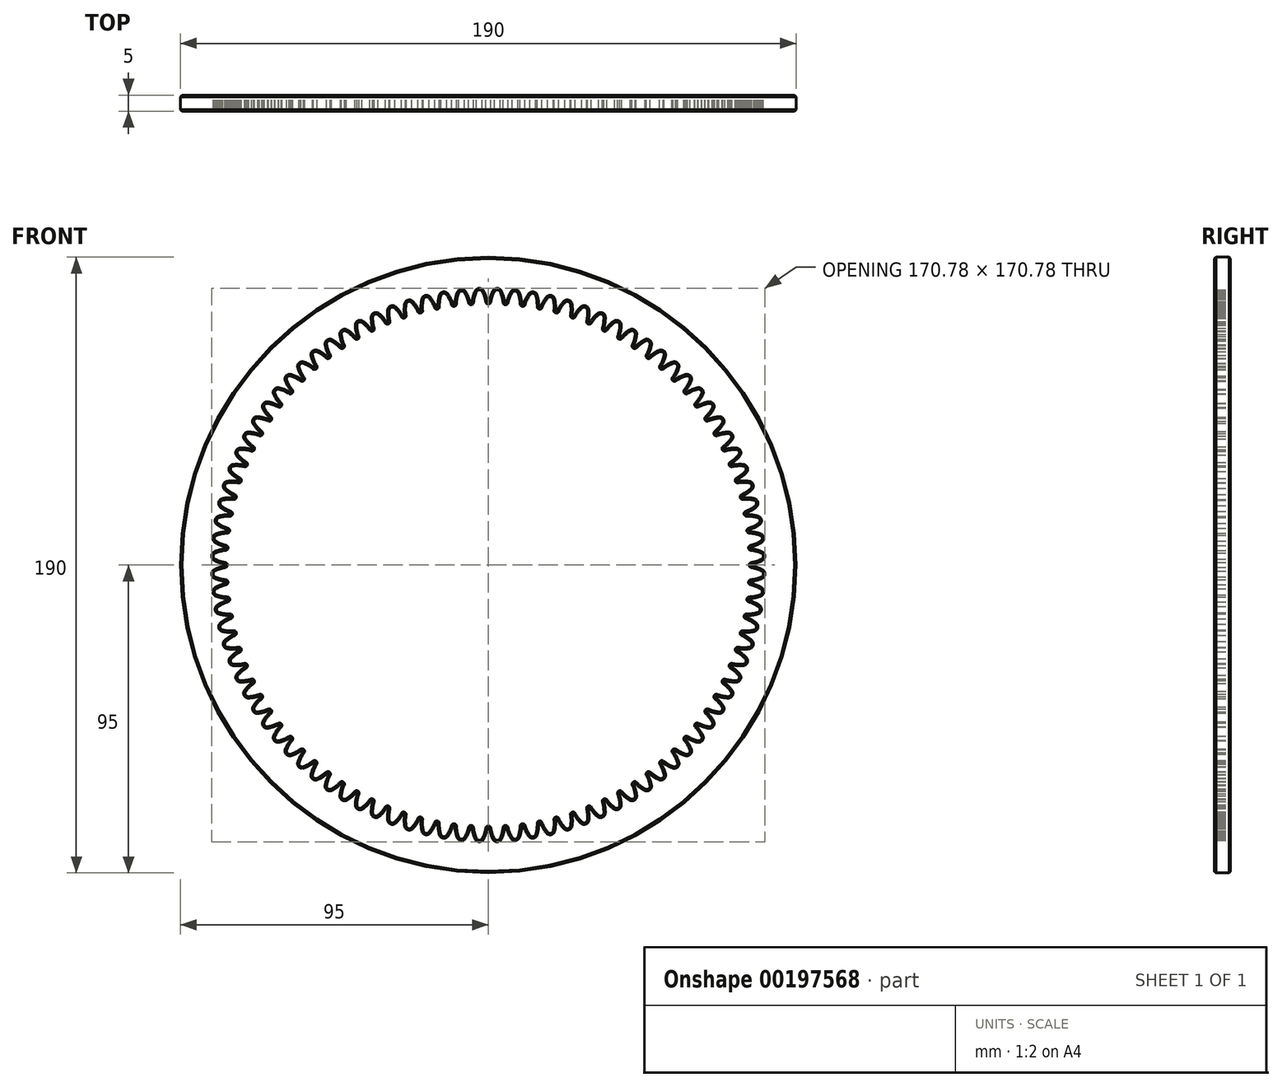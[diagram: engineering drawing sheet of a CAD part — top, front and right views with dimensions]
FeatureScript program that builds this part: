
annotation { "Feature Type Name" : "Feature", "Feature Type Description" : "" }
export const myFeature = defineFeature(function(context is Context, id is Id, definition is map)
    precondition{}
    {
        {
            var Q0;
            Q0=qCreatedBy(makeId("Front.planeOp"),FACE);
            var sketch = newSketch(context, id + "F0", { "sketchPlane" : qUnion([Q0])});
            skArc(sketch, "E0.1.2", {"start": v(-3.67, 84.28) * mm, "mid": v(-4.24, 82.62) * mm, "end": v(-4.54, 80.9) * mm});
            skArc(sketch, "E1.MirrorCS", {"start": v(-1.85, 84.33) * mm, "mid": v(-1.17, 82.72) * mm, "end": v(-0.76, 81.02) * mm});
            skArc(sketch, "E2", {"start": v(-0.76, 81.02) * mm, "mid": v(0, 80.48) * mm, "end": v(0.76, 81.02) * mm});
            skArc(sketch, "E3", {"start": v(-1.85, 84.33) * mm, "mid": v(-2.78, 84.9) * mm, "end": v(-3.67, 84.28) * mm});
            skArc(sketch, "E4.1.0", {"start": v(-6.06, 80.8) * mm, "mid": v(-5.26, 80.3) * mm, "end": v(-4.54, 80.9) * mm});
            skArc(sketch, "E4.1.1", {"start": v(-9.17, 83.85) * mm, "mid": v(-9.64, 82.17) * mm, "end": v(-9.82, 80.43) * mm});
            skArc(sketch, "E4.1.2", {"start": v(-7.36, 84.03) * mm, "mid": v(-6.58, 82.47) * mm, "end": v(-6.06, 80.8) * mm});
            skArc(sketch, "E4.1.3", {"start": v(-7.36, 84.03) * mm, "mid": v(-8.33, 84.53) * mm, "end": v(-9.17, 83.85) * mm});
            skArc(sketch, "E4.2.0", {"start": v(-11.33, 80.23) * mm, "mid": v(-10.5, 79.79) * mm, "end": v(-9.82, 80.43) * mm});
            skArc(sketch, "E4.2.1", {"start": v(-14.64, 83.08) * mm, "mid": v(-14.99, 81.36) * mm, "end": v(-15.06, 79.62) * mm});
            skArc(sketch, "E4.2.2", {"start": v(-12.84, 83.37) * mm, "mid": v(-11.96, 81.86) * mm, "end": v(-11.33, 80.23) * mm});
            skArc(sketch, "E4.2.3", {"start": v(-12.84, 83.37) * mm, "mid": v(-13.84, 83.8) * mm, "end": v(-14.64, 83.08) * mm});
            skArc(sketch, "E4.3.0", {"start": v(-16.56, 79.32) * mm, "mid": v(-15.7, 78.93) * mm, "end": v(-15.06, 79.62) * mm});
            skArc(sketch, "E4.3.1", {"start": v(-20.04, 81.94) * mm, "mid": v(-20.28, 80.2) * mm, "end": v(-20.23, 78.46) * mm});
            skArc(sketch, "E4.3.2", {"start": v(-18.27, 82.35) * mm, "mid": v(-17.29, 80.9) * mm, "end": v(-16.56, 79.32) * mm});
            skArc(sketch, "E4.3.3", {"start": v(-18.27, 82.35) * mm, "mid": v(-19.29, 82.72) * mm, "end": v(-20.04, 81.94) * mm});
            skArc(sketch, "E4.4.0", {"start": v(-21.7, 78.07) * mm, "mid": v(-20.83, 77.73) * mm, "end": v(-20.23, 78.46) * mm});
            skArc(sketch, "E4.4.1", {"start": v(-25.35, 80.45) * mm, "mid": v(-25.48, 78.71) * mm, "end": v(-25.32, 76.97) * mm});
            skArc(sketch, "E4.4.2", {"start": v(-23.62, 80.98) * mm, "mid": v(-22.54, 79.6) * mm, "end": v(-21.7, 78.07) * mm});
            skArc(sketch, "E4.4.3", {"start": v(-23.62, 80.98) * mm, "mid": v(-24.66, 81.28) * mm, "end": v(-25.35, 80.45) * mm});
            skArc(sketch, "E4.5.0", {"start": v(-26.77, 76.48) * mm, "mid": v(-25.87, 76.2) * mm, "end": v(-25.32, 76.97) * mm});
            skArc(sketch, "E4.5.1", {"start": v(-30.56, 78.62) * mm, "mid": v(-30.58, 76.88) * mm, "end": v(-30.3, 75.15) * mm});
            skArc(sketch, "E4.5.2", {"start": v(-28.86, 79.26) * mm, "mid": v(-27.7, 77.96) * mm, "end": v(-26.77, 76.48) * mm});
            skArc(sketch, "E4.5.3", {"start": v(-28.86, 79.26) * mm, "mid": v(-29.92, 79.5) * mm, "end": v(-30.56, 78.62) * mm});
            skArc(sketch, "E4.6.0", {"start": v(-31.71, 74.56) * mm, "mid": v(-30.8, 74.35) * mm, "end": v(-30.3, 75.15) * mm});
            skArc(sketch, "E4.6.1", {"start": v(-35.64, 76.46) * mm, "mid": v(-35.54, 74.71) * mm, "end": v(-35.15, 73) * mm});
            skArc(sketch, "E4.6.2", {"start": v(-33.99, 77.2) * mm, "mid": v(-32.74, 75.98) * mm, "end": v(-31.71, 74.56) * mm});
            skArc(sketch, "E4.6.3", {"start": v(-33.99, 77.2) * mm, "mid": v(-35.05, 77.37) * mm, "end": v(-35.64, 76.46) * mm});
            skArc(sketch, "E4.7.0", {"start": v(-36.52, 72.33) * mm, "mid": v(-35.6, 72.18) * mm, "end": v(-35.15, 73) * mm});
            skArc(sketch, "E4.7.1", {"start": v(-40.56, 73.96) * mm, "mid": v(-40.35, 72.23) * mm, "end": v(-39.85, 70.55) * mm});
            skArc(sketch, "E4.7.2", {"start": v(-38.96, 74.82) * mm, "mid": v(-37.64, 73.68) * mm, "end": v(-36.52, 72.33) * mm});
            skArc(sketch, "E4.7.3", {"start": v(-38.96, 74.82) * mm, "mid": v(-40.04, 74.9) * mm, "end": v(-40.56, 73.96) * mm});
            skArc(sketch, "E4.8.0", {"start": v(-41.17, 69.79) * mm, "mid": v(-40.24, 69.7) * mm, "end": v(-39.85, 70.55) * mm});
            skArc(sketch, "E4.8.1", {"start": v(-45.31, 71.15) * mm, "mid": v(-44.99, 69.43) * mm, "end": v(-44.38, 67.8) * mm});
            skArc(sketch, "E4.8.2", {"start": v(-43.77, 72.1) * mm, "mid": v(-42.38, 71.06) * mm, "end": v(-41.17, 69.79) * mm});
            skArc(sketch, "E4.8.3", {"start": v(-43.77, 72.1) * mm, "mid": v(-44.85, 72.13) * mm, "end": v(-45.31, 71.15) * mm});
            skArc(sketch, "E4.9.0", {"start": v(-45.65, 66.94) * mm, "mid": v(-44.7, 66.91) * mm, "end": v(-44.38, 67.8) * mm});
            skArc(sketch, "E4.9.1", {"start": v(-49.87, 68.04) * mm, "mid": v(-49.43, 66.34) * mm, "end": v(-48.72, 64.75) * mm});
            skArc(sketch, "E4.9.2", {"start": v(-48.4, 69.1) * mm, "mid": v(-46.93, 68.13) * mm, "end": v(-45.65, 66.94) * mm});
            skArc(sketch, "E4.9.3", {"start": v(-48.4, 69.1) * mm, "mid": v(-49.47, 69.04) * mm, "end": v(-49.87, 68.04) * mm});
            skArc(sketch, "E4.10.0", {"start": v(-49.93, 63.82) * mm, "mid": v(-49, 63.85) * mm, "end": v(-48.72, 64.75) * mm});
            skArc(sketch, "E4.10.1", {"start": v(-54.21, 64.63) * mm, "mid": v(-53.66, 62.97) * mm, "end": v(-52.85, 61.42) * mm});
            skArc(sketch, "E4.10.2", {"start": v(-52.8, 65.78) * mm, "mid": v(-51.29, 64.92) * mm, "end": v(-49.93, 63.82) * mm});
            skArc(sketch, "E4.10.3", {"start": v(-52.8, 65.78) * mm, "mid": v(-53.88, 65.66) * mm, "end": v(-54.21, 64.63) * mm});
            skArc(sketch, "E4.11.0", {"start": v(-54, 60.41) * mm, "mid": v(-53.06, 60.5) * mm, "end": v(-52.85, 61.42) * mm});
            skArc(sketch, "E4.11.1", {"start": v(-58.32, 60.94) * mm, "mid": v(-57.67, 59.32) * mm, "end": v(-56.75, 57.83) * mm});
            skArc(sketch, "E4.11.2", {"start": v(-57, 62.18) * mm, "mid": v(-55.43, 61.42) * mm, "end": v(-54, 60.41) * mm});
            skArc(sketch, "E4.11.3", {"start": v(-57, 62.18) * mm, "mid": v(-58.06, 62) * mm, "end": v(-58.32, 60.94) * mm});
            skArc(sketch, "E4.12.0", {"start": v(-57.83, 56.75) * mm, "mid": v(-56.9, 56.9) * mm, "end": v(-56.75, 57.83) * mm});
            skArc(sketch, "E4.12.1", {"start": v(-62.18, 57) * mm, "mid": v(-61.42, 55.43) * mm, "end": v(-60.41, 54) * mm});
            skArc(sketch, "E4.12.2", {"start": v(-60.94, 58.32) * mm, "mid": v(-59.32, 57.67) * mm, "end": v(-57.83, 56.75) * mm});
            skArc(sketch, "E4.12.3", {"start": v(-60.94, 58.32) * mm, "mid": v(-62, 58.06) * mm, "end": v(-62.18, 57) * mm});
            skArc(sketch, "E4.13.0", {"start": v(-61.42, 52.85) * mm, "mid": v(-60.5, 53.06) * mm, "end": v(-60.41, 54) * mm});
            skArc(sketch, "E4.13.1", {"start": v(-65.78, 52.8) * mm, "mid": v(-64.92, 51.29) * mm, "end": v(-63.82, 49.93) * mm});
            skArc(sketch, "E4.13.2", {"start": v(-64.63, 54.21) * mm, "mid": v(-62.97, 53.66) * mm, "end": v(-61.42, 52.85) * mm});
            skArc(sketch, "E4.13.3", {"start": v(-64.63, 54.21) * mm, "mid": v(-65.66, 53.88) * mm, "end": v(-65.78, 52.8) * mm});
            skArc(sketch, "E4.14.0", {"start": v(-64.75, 48.72) * mm, "mid": v(-63.85, 49) * mm, "end": v(-63.82, 49.93) * mm});
            skArc(sketch, "E4.14.1", {"start": v(-69.1, 48.4) * mm, "mid": v(-68.13, 46.93) * mm, "end": v(-66.94, 45.65) * mm});
            skArc(sketch, "E4.14.2", {"start": v(-68.04, 49.87) * mm, "mid": v(-66.34, 49.43) * mm, "end": v(-64.75, 48.72) * mm});
            skArc(sketch, "E4.14.3", {"start": v(-68.04, 49.87) * mm, "mid": v(-69.04, 49.47) * mm, "end": v(-69.1, 48.4) * mm});
            skArc(sketch, "E4.15.0", {"start": v(-67.8, 44.38) * mm, "mid": v(-66.91, 44.7) * mm, "end": v(-66.94, 45.65) * mm});
            skArc(sketch, "E4.15.1", {"start": v(-72.1, 43.77) * mm, "mid": v(-71.06, 42.38) * mm, "end": v(-69.79, 41.17) * mm});
            skArc(sketch, "E4.15.2", {"start": v(-71.15, 45.31) * mm, "mid": v(-69.43, 44.99) * mm, "end": v(-67.8, 44.38) * mm});
            skArc(sketch, "E4.15.3", {"start": v(-71.15, 45.31) * mm, "mid": v(-72.13, 44.85) * mm, "end": v(-72.1, 43.77) * mm});
            skArc(sketch, "E4.16.0", {"start": v(-70.55, 39.85) * mm, "mid": v(-69.7, 40.24) * mm, "end": v(-69.79, 41.17) * mm});
            skArc(sketch, "E4.16.1", {"start": v(-74.82, 38.96) * mm, "mid": v(-73.68, 37.64) * mm, "end": v(-72.33, 36.52) * mm});
            skArc(sketch, "E4.16.2", {"start": v(-73.96, 40.56) * mm, "mid": v(-72.23, 40.35) * mm, "end": v(-70.55, 39.85) * mm});
            skArc(sketch, "E4.16.3", {"start": v(-73.96, 40.56) * mm, "mid": v(-74.9, 40.04) * mm, "end": v(-74.82, 38.96) * mm});
            skArc(sketch, "E4.17.0", {"start": v(-73, 35.15) * mm, "mid": v(-72.18, 35.6) * mm, "end": v(-72.33, 36.52) * mm});
            skArc(sketch, "E4.17.1", {"start": v(-77.2, 33.99) * mm, "mid": v(-75.98, 32.74) * mm, "end": v(-74.56, 31.71) * mm});
            skArc(sketch, "E4.17.2", {"start": v(-76.46, 35.64) * mm, "mid": v(-74.71, 35.54) * mm, "end": v(-73, 35.15) * mm});
            skArc(sketch, "E4.17.3", {"start": v(-76.46, 35.64) * mm, "mid": v(-77.37, 35.05) * mm, "end": v(-77.2, 33.99) * mm});
            skArc(sketch, "E4.18.0", {"start": v(-75.15, 30.3) * mm, "mid": v(-74.35, 30.8) * mm, "end": v(-74.56, 31.71) * mm});
            skArc(sketch, "E4.18.1", {"start": v(-79.26, 28.86) * mm, "mid": v(-77.96, 27.7) * mm, "end": v(-76.48, 26.77) * mm});
            skArc(sketch, "E4.18.2", {"start": v(-78.62, 30.56) * mm, "mid": v(-76.88, 30.58) * mm, "end": v(-75.15, 30.3) * mm});
            skArc(sketch, "E4.18.3", {"start": v(-78.62, 30.56) * mm, "mid": v(-79.5, 29.92) * mm, "end": v(-79.26, 28.86) * mm});
            skArc(sketch, "E4.19.0", {"start": v(-76.97, 25.32) * mm, "mid": v(-76.2, 25.87) * mm, "end": v(-76.48, 26.77) * mm});
            skArc(sketch, "E4.19.1", {"start": v(-80.98, 23.62) * mm, "mid": v(-79.6, 22.54) * mm, "end": v(-78.07, 21.7) * mm});
            skArc(sketch, "E4.19.2", {"start": v(-80.45, 25.35) * mm, "mid": v(-78.71, 25.48) * mm, "end": v(-76.97, 25.32) * mm});
            skArc(sketch, "E4.19.3", {"start": v(-80.45, 25.35) * mm, "mid": v(-81.28, 24.66) * mm, "end": v(-80.98, 23.62) * mm});
            skArc(sketch, "E4.20.0", {"start": v(-78.46, 20.23) * mm, "mid": v(-77.73, 20.83) * mm, "end": v(-78.07, 21.7) * mm});
            skArc(sketch, "E4.20.1", {"start": v(-82.35, 18.27) * mm, "mid": v(-80.9, 17.29) * mm, "end": v(-79.32, 16.56) * mm});
            skArc(sketch, "E4.20.2", {"start": v(-81.94, 20.04) * mm, "mid": v(-80.2, 20.28) * mm, "end": v(-78.46, 20.23) * mm});
            skArc(sketch, "E4.20.3", {"start": v(-81.94, 20.04) * mm, "mid": v(-82.72, 19.29) * mm, "end": v(-82.35, 18.27) * mm});
            skArc(sketch, "E4.21.0", {"start": v(-79.62, 15.06) * mm, "mid": v(-78.93, 15.7) * mm, "end": v(-79.32, 16.56) * mm});
            skArc(sketch, "E4.21.1", {"start": v(-83.37, 12.84) * mm, "mid": v(-81.86, 11.96) * mm, "end": v(-80.23, 11.33) * mm});
            skArc(sketch, "E4.21.2", {"start": v(-83.08, 14.64) * mm, "mid": v(-81.36, 14.99) * mm, "end": v(-79.62, 15.06) * mm});
            skArc(sketch, "E4.21.3", {"start": v(-83.08, 14.64) * mm, "mid": v(-83.8, 13.84) * mm, "end": v(-83.37, 12.84) * mm});
            skArc(sketch, "E4.22.0", {"start": v(-80.43, 9.82) * mm, "mid": v(-79.79, 10.5) * mm, "end": v(-80.23, 11.33) * mm});
            skArc(sketch, "E4.22.1", {"start": v(-84.03, 7.36) * mm, "mid": v(-82.47, 6.58) * mm, "end": v(-80.8, 6.06) * mm});
            skArc(sketch, "E4.22.2", {"start": v(-83.85, 9.17) * mm, "mid": v(-82.17, 9.64) * mm, "end": v(-80.43, 9.82) * mm});
            skArc(sketch, "E4.22.3", {"start": v(-83.85, 9.17) * mm, "mid": v(-84.53, 8.33) * mm, "end": v(-84.03, 7.36) * mm});
            skArc(sketch, "E4.23.0", {"start": v(-80.9, 4.54) * mm, "mid": v(-80.3, 5.26) * mm, "end": v(-80.8, 6.06) * mm});
            skArc(sketch, "E4.23.1", {"start": v(-84.33, 1.85) * mm, "mid": v(-82.72, 1.17) * mm, "end": v(-81.02, 0.76) * mm});
            skArc(sketch, "E4.23.2", {"start": v(-84.28, 3.67) * mm, "mid": v(-82.62, 4.24) * mm, "end": v(-80.9, 4.54) * mm});
            skArc(sketch, "E4.23.3", {"start": v(-84.28, 3.67) * mm, "mid": v(-84.9, 2.78) * mm, "end": v(-84.33, 1.85) * mm});
            skArc(sketch, "E4.24.0", {"start": v(-81.02, -0.76) * mm, "mid": v(-80.48, 0) * mm, "end": v(-81.02, 0.76) * mm});
            skArc(sketch, "E4.24.1", {"start": v(-84.28, -3.67) * mm, "mid": v(-82.62, -4.24) * mm, "end": v(-80.9, -4.54) * mm});
            skArc(sketch, "E4.24.2", {"start": v(-84.33, -1.85) * mm, "mid": v(-82.72, -1.17) * mm, "end": v(-81.02, -0.76) * mm});
            skArc(sketch, "E4.24.3", {"start": v(-84.33, -1.85) * mm, "mid": v(-84.9, -2.78) * mm, "end": v(-84.28, -3.67) * mm});
            skArc(sketch, "E4.25.0", {"start": v(-80.8, -6.06) * mm, "mid": v(-80.3, -5.26) * mm, "end": v(-80.9, -4.54) * mm});
            skArc(sketch, "E4.25.1", {"start": v(-83.85, -9.17) * mm, "mid": v(-82.17, -9.64) * mm, "end": v(-80.43, -9.82) * mm});
            skArc(sketch, "E4.25.2", {"start": v(-84.03, -7.36) * mm, "mid": v(-82.47, -6.58) * mm, "end": v(-80.8, -6.06) * mm});
            skArc(sketch, "E4.25.3", {"start": v(-84.03, -7.36) * mm, "mid": v(-84.53, -8.33) * mm, "end": v(-83.85, -9.17) * mm});
            skArc(sketch, "E4.26.0", {"start": v(-80.23, -11.33) * mm, "mid": v(-79.79, -10.5) * mm, "end": v(-80.43, -9.82) * mm});
            skArc(sketch, "E4.26.1", {"start": v(-83.08, -14.64) * mm, "mid": v(-81.36, -14.99) * mm, "end": v(-79.62, -15.06) * mm});
            skArc(sketch, "E4.26.2", {"start": v(-83.37, -12.84) * mm, "mid": v(-81.86, -11.96) * mm, "end": v(-80.23, -11.33) * mm});
            skArc(sketch, "E4.26.3", {"start": v(-83.37, -12.84) * mm, "mid": v(-83.8, -13.84) * mm, "end": v(-83.08, -14.64) * mm});
            skArc(sketch, "E4.27.0", {"start": v(-79.32, -16.56) * mm, "mid": v(-78.93, -15.7) * mm, "end": v(-79.62, -15.06) * mm});
            skArc(sketch, "E4.27.1", {"start": v(-81.94, -20.04) * mm, "mid": v(-80.2, -20.28) * mm, "end": v(-78.46, -20.23) * mm});
            skArc(sketch, "E4.27.2", {"start": v(-82.35, -18.27) * mm, "mid": v(-80.9, -17.29) * mm, "end": v(-79.32, -16.56) * mm});
            skArc(sketch, "E4.27.3", {"start": v(-82.35, -18.27) * mm, "mid": v(-82.72, -19.29) * mm, "end": v(-81.94, -20.04) * mm});
            skArc(sketch, "E4.28.0", {"start": v(-78.07, -21.7) * mm, "mid": v(-77.73, -20.83) * mm, "end": v(-78.46, -20.23) * mm});
            skArc(sketch, "E4.28.1", {"start": v(-80.45, -25.35) * mm, "mid": v(-78.71, -25.48) * mm, "end": v(-76.97, -25.32) * mm});
            skArc(sketch, "E4.28.2", {"start": v(-80.98, -23.62) * mm, "mid": v(-79.6, -22.54) * mm, "end": v(-78.07, -21.7) * mm});
            skArc(sketch, "E4.28.3", {"start": v(-80.98, -23.62) * mm, "mid": v(-81.28, -24.66) * mm, "end": v(-80.45, -25.35) * mm});
            skArc(sketch, "E4.29.0", {"start": v(-76.48, -26.77) * mm, "mid": v(-76.2, -25.87) * mm, "end": v(-76.97, -25.32) * mm});
            skArc(sketch, "E4.29.1", {"start": v(-78.62, -30.56) * mm, "mid": v(-76.88, -30.58) * mm, "end": v(-75.15, -30.3) * mm});
            skArc(sketch, "E4.29.2", {"start": v(-79.26, -28.86) * mm, "mid": v(-77.96, -27.7) * mm, "end": v(-76.48, -26.77) * mm});
            skArc(sketch, "E4.29.3", {"start": v(-79.26, -28.86) * mm, "mid": v(-79.5, -29.92) * mm, "end": v(-78.62, -30.56) * mm});
            skArc(sketch, "E4.30.0", {"start": v(-74.56, -31.71) * mm, "mid": v(-74.35, -30.8) * mm, "end": v(-75.15, -30.3) * mm});
            skArc(sketch, "E4.30.1", {"start": v(-76.46, -35.64) * mm, "mid": v(-74.71, -35.54) * mm, "end": v(-73, -35.15) * mm});
            skArc(sketch, "E4.30.2", {"start": v(-77.2, -33.99) * mm, "mid": v(-75.98, -32.74) * mm, "end": v(-74.56, -31.71) * mm});
            skArc(sketch, "E4.30.3", {"start": v(-77.2, -33.99) * mm, "mid": v(-77.37, -35.05) * mm, "end": v(-76.46, -35.64) * mm});
            skArc(sketch, "E4.31.0", {"start": v(-72.33, -36.52) * mm, "mid": v(-72.18, -35.6) * mm, "end": v(-73, -35.15) * mm});
            skArc(sketch, "E4.31.1", {"start": v(-73.96, -40.56) * mm, "mid": v(-72.23, -40.35) * mm, "end": v(-70.55, -39.85) * mm});
            skArc(sketch, "E4.31.2", {"start": v(-74.82, -38.96) * mm, "mid": v(-73.68, -37.64) * mm, "end": v(-72.33, -36.52) * mm});
            skArc(sketch, "E4.31.3", {"start": v(-74.82, -38.96) * mm, "mid": v(-74.9, -40.04) * mm, "end": v(-73.96, -40.56) * mm});
            skArc(sketch, "E4.32.0", {"start": v(-69.79, -41.17) * mm, "mid": v(-69.7, -40.24) * mm, "end": v(-70.55, -39.85) * mm});
            skArc(sketch, "E4.32.1", {"start": v(-71.15, -45.31) * mm, "mid": v(-69.43, -44.99) * mm, "end": v(-67.8, -44.38) * mm});
            skArc(sketch, "E4.32.2", {"start": v(-72.1, -43.77) * mm, "mid": v(-71.06, -42.38) * mm, "end": v(-69.79, -41.17) * mm});
            skArc(sketch, "E4.32.3", {"start": v(-72.1, -43.77) * mm, "mid": v(-72.13, -44.85) * mm, "end": v(-71.15, -45.31) * mm});
            skArc(sketch, "E4.33.0", {"start": v(-66.94, -45.65) * mm, "mid": v(-66.91, -44.7) * mm, "end": v(-67.8, -44.38) * mm});
            skArc(sketch, "E4.33.1", {"start": v(-68.04, -49.87) * mm, "mid": v(-66.34, -49.43) * mm, "end": v(-64.75, -48.72) * mm});
            skArc(sketch, "E4.33.2", {"start": v(-69.1, -48.4) * mm, "mid": v(-68.13, -46.93) * mm, "end": v(-66.94, -45.65) * mm});
            skArc(sketch, "E4.33.3", {"start": v(-69.1, -48.4) * mm, "mid": v(-69.04, -49.47) * mm, "end": v(-68.04, -49.87) * mm});
            skArc(sketch, "E4.34.0", {"start": v(-63.82, -49.93) * mm, "mid": v(-63.85, -49) * mm, "end": v(-64.75, -48.72) * mm});
            skArc(sketch, "E4.34.1", {"start": v(-64.63, -54.21) * mm, "mid": v(-62.97, -53.66) * mm, "end": v(-61.42, -52.85) * mm});
            skArc(sketch, "E4.34.2", {"start": v(-65.78, -52.8) * mm, "mid": v(-64.92, -51.29) * mm, "end": v(-63.82, -49.93) * mm});
            skArc(sketch, "E4.34.3", {"start": v(-65.78, -52.8) * mm, "mid": v(-65.66, -53.88) * mm, "end": v(-64.63, -54.21) * mm});
            skArc(sketch, "E4.35.0", {"start": v(-60.41, -54) * mm, "mid": v(-60.5, -53.06) * mm, "end": v(-61.42, -52.85) * mm});
            skArc(sketch, "E4.35.1", {"start": v(-60.94, -58.32) * mm, "mid": v(-59.32, -57.67) * mm, "end": v(-57.83, -56.75) * mm});
            skArc(sketch, "E4.35.2", {"start": v(-62.18, -57) * mm, "mid": v(-61.42, -55.43) * mm, "end": v(-60.41, -54) * mm});
            skArc(sketch, "E4.35.3", {"start": v(-62.18, -57) * mm, "mid": v(-62, -58.06) * mm, "end": v(-60.94, -58.32) * mm});
            skArc(sketch, "E4.36.0", {"start": v(-56.75, -57.83) * mm, "mid": v(-56.9, -56.9) * mm, "end": v(-57.83, -56.75) * mm});
            skArc(sketch, "E4.36.1", {"start": v(-57, -62.18) * mm, "mid": v(-55.43, -61.42) * mm, "end": v(-54, -60.41) * mm});
            skArc(sketch, "E4.36.2", {"start": v(-58.32, -60.94) * mm, "mid": v(-57.67, -59.32) * mm, "end": v(-56.75, -57.83) * mm});
            skArc(sketch, "E4.36.3", {"start": v(-58.32, -60.94) * mm, "mid": v(-58.06, -62) * mm, "end": v(-57, -62.18) * mm});
            skArc(sketch, "E4.37.0", {"start": v(-52.85, -61.42) * mm, "mid": v(-53.06, -60.5) * mm, "end": v(-54, -60.41) * mm});
            skArc(sketch, "E4.37.1", {"start": v(-52.8, -65.78) * mm, "mid": v(-51.29, -64.92) * mm, "end": v(-49.93, -63.82) * mm});
            skArc(sketch, "E4.37.2", {"start": v(-54.21, -64.63) * mm, "mid": v(-53.66, -62.97) * mm, "end": v(-52.85, -61.42) * mm});
            skArc(sketch, "E4.37.3", {"start": v(-54.21, -64.63) * mm, "mid": v(-53.88, -65.66) * mm, "end": v(-52.8, -65.78) * mm});
            skArc(sketch, "E4.38.0", {"start": v(-48.72, -64.75) * mm, "mid": v(-49, -63.85) * mm, "end": v(-49.93, -63.82) * mm});
            skArc(sketch, "E4.38.1", {"start": v(-48.4, -69.1) * mm, "mid": v(-46.93, -68.13) * mm, "end": v(-45.65, -66.94) * mm});
            skArc(sketch, "E4.38.2", {"start": v(-49.87, -68.04) * mm, "mid": v(-49.43, -66.34) * mm, "end": v(-48.72, -64.75) * mm});
            skArc(sketch, "E4.38.3", {"start": v(-49.87, -68.04) * mm, "mid": v(-49.47, -69.04) * mm, "end": v(-48.4, -69.1) * mm});
            skArc(sketch, "E4.39.0", {"start": v(-44.38, -67.8) * mm, "mid": v(-44.7, -66.91) * mm, "end": v(-45.65, -66.94) * mm});
            skArc(sketch, "E4.39.1", {"start": v(-43.77, -72.1) * mm, "mid": v(-42.38, -71.06) * mm, "end": v(-41.17, -69.79) * mm});
            skArc(sketch, "E4.39.2", {"start": v(-45.31, -71.15) * mm, "mid": v(-44.99, -69.43) * mm, "end": v(-44.38, -67.8) * mm});
            skArc(sketch, "E4.39.3", {"start": v(-45.31, -71.15) * mm, "mid": v(-44.85, -72.13) * mm, "end": v(-43.77, -72.1) * mm});
            skArc(sketch, "E4.40.0", {"start": v(-39.85, -70.55) * mm, "mid": v(-40.24, -69.7) * mm, "end": v(-41.17, -69.79) * mm});
            skArc(sketch, "E4.40.1", {"start": v(-38.96, -74.82) * mm, "mid": v(-37.64, -73.68) * mm, "end": v(-36.52, -72.33) * mm});
            skArc(sketch, "E4.40.2", {"start": v(-40.56, -73.96) * mm, "mid": v(-40.35, -72.23) * mm, "end": v(-39.85, -70.55) * mm});
            skArc(sketch, "E4.40.3", {"start": v(-40.56, -73.96) * mm, "mid": v(-40.04, -74.9) * mm, "end": v(-38.96, -74.82) * mm});
            skArc(sketch, "E4.41.0", {"start": v(-35.15, -73) * mm, "mid": v(-35.6, -72.18) * mm, "end": v(-36.52, -72.33) * mm});
            skArc(sketch, "E4.41.1", {"start": v(-33.99, -77.2) * mm, "mid": v(-32.74, -75.98) * mm, "end": v(-31.71, -74.56) * mm});
            skArc(sketch, "E4.41.2", {"start": v(-35.64, -76.46) * mm, "mid": v(-35.54, -74.71) * mm, "end": v(-35.15, -73) * mm});
            skArc(sketch, "E4.41.3", {"start": v(-35.64, -76.46) * mm, "mid": v(-35.05, -77.37) * mm, "end": v(-33.99, -77.2) * mm});
            skArc(sketch, "E4.42.0", {"start": v(-30.3, -75.15) * mm, "mid": v(-30.8, -74.35) * mm, "end": v(-31.71, -74.56) * mm});
            skArc(sketch, "E4.42.1", {"start": v(-28.86, -79.26) * mm, "mid": v(-27.7, -77.96) * mm, "end": v(-26.77, -76.48) * mm});
            skArc(sketch, "E4.42.2", {"start": v(-30.56, -78.62) * mm, "mid": v(-30.58, -76.88) * mm, "end": v(-30.3, -75.15) * mm});
            skArc(sketch, "E4.42.3", {"start": v(-30.56, -78.62) * mm, "mid": v(-29.92, -79.5) * mm, "end": v(-28.86, -79.26) * mm});
            skArc(sketch, "E4.43.0", {"start": v(-25.32, -76.97) * mm, "mid": v(-25.87, -76.2) * mm, "end": v(-26.77, -76.48) * mm});
            skArc(sketch, "E4.43.1", {"start": v(-23.62, -80.98) * mm, "mid": v(-22.54, -79.6) * mm, "end": v(-21.7, -78.07) * mm});
            skArc(sketch, "E4.43.2", {"start": v(-25.35, -80.45) * mm, "mid": v(-25.48, -78.71) * mm, "end": v(-25.32, -76.97) * mm});
            skArc(sketch, "E4.43.3", {"start": v(-25.35, -80.45) * mm, "mid": v(-24.66, -81.28) * mm, "end": v(-23.62, -80.98) * mm});
            skArc(sketch, "E4.44.0", {"start": v(-20.23, -78.46) * mm, "mid": v(-20.83, -77.73) * mm, "end": v(-21.7, -78.07) * mm});
            skArc(sketch, "E4.44.1", {"start": v(-18.27, -82.35) * mm, "mid": v(-17.29, -80.9) * mm, "end": v(-16.56, -79.32) * mm});
            skArc(sketch, "E4.44.2", {"start": v(-20.04, -81.94) * mm, "mid": v(-20.28, -80.2) * mm, "end": v(-20.23, -78.46) * mm});
            skArc(sketch, "E4.44.3", {"start": v(-20.04, -81.94) * mm, "mid": v(-19.29, -82.72) * mm, "end": v(-18.27, -82.35) * mm});
            skArc(sketch, "E4.45.0", {"start": v(-15.06, -79.62) * mm, "mid": v(-15.7, -78.93) * mm, "end": v(-16.56, -79.32) * mm});
            skArc(sketch, "E4.45.1", {"start": v(-12.84, -83.37) * mm, "mid": v(-11.96, -81.86) * mm, "end": v(-11.33, -80.23) * mm});
            skArc(sketch, "E4.45.2", {"start": v(-14.64, -83.08) * mm, "mid": v(-14.99, -81.36) * mm, "end": v(-15.06, -79.62) * mm});
            skArc(sketch, "E4.45.3", {"start": v(-14.64, -83.08) * mm, "mid": v(-13.84, -83.8) * mm, "end": v(-12.84, -83.37) * mm});
            skArc(sketch, "E4.46.0", {"start": v(-9.82, -80.43) * mm, "mid": v(-10.5, -79.79) * mm, "end": v(-11.33, -80.23) * mm});
            skArc(sketch, "E4.46.1", {"start": v(-7.36, -84.03) * mm, "mid": v(-6.58, -82.47) * mm, "end": v(-6.06, -80.8) * mm});
            skArc(sketch, "E4.46.2", {"start": v(-9.17, -83.85) * mm, "mid": v(-9.64, -82.17) * mm, "end": v(-9.82, -80.43) * mm});
            skArc(sketch, "E4.46.3", {"start": v(-9.17, -83.85) * mm, "mid": v(-8.33, -84.53) * mm, "end": v(-7.36, -84.03) * mm});
            skArc(sketch, "E4.47.0", {"start": v(-4.54, -80.9) * mm, "mid": v(-5.26, -80.3) * mm, "end": v(-6.06, -80.8) * mm});
            skArc(sketch, "E4.47.1", {"start": v(-1.85, -84.33) * mm, "mid": v(-1.17, -82.72) * mm, "end": v(-0.76, -81.02) * mm});
            skArc(sketch, "E4.47.2", {"start": v(-3.67, -84.28) * mm, "mid": v(-4.24, -82.62) * mm, "end": v(-4.54, -80.9) * mm});
            skArc(sketch, "E4.47.3", {"start": v(-3.67, -84.28) * mm, "mid": v(-2.78, -84.9) * mm, "end": v(-1.85, -84.33) * mm});
            skArc(sketch, "E4.48.0", {"start": v(0.76, -81.02) * mm, "mid": v(0, -80.48) * mm, "end": v(-0.76, -81.02) * mm});
            skArc(sketch, "E4.48.1", {"start": v(3.67, -84.28) * mm, "mid": v(4.24, -82.62) * mm, "end": v(4.54, -80.9) * mm});
            skArc(sketch, "E4.48.2", {"start": v(1.85, -84.33) * mm, "mid": v(1.17, -82.72) * mm, "end": v(0.76, -81.02) * mm});
            skArc(sketch, "E4.48.3", {"start": v(1.85, -84.33) * mm, "mid": v(2.78, -84.9) * mm, "end": v(3.67, -84.28) * mm});
            skArc(sketch, "E4.49.0", {"start": v(6.06, -80.8) * mm, "mid": v(5.26, -80.3) * mm, "end": v(4.54, -80.9) * mm});
            skArc(sketch, "E4.49.1", {"start": v(9.17, -83.85) * mm, "mid": v(9.64, -82.17) * mm, "end": v(9.82, -80.43) * mm});
            skArc(sketch, "E4.49.2", {"start": v(7.36, -84.03) * mm, "mid": v(6.58, -82.47) * mm, "end": v(6.06, -80.8) * mm});
            skArc(sketch, "E4.49.3", {"start": v(7.36, -84.03) * mm, "mid": v(8.33, -84.53) * mm, "end": v(9.17, -83.85) * mm});
            skArc(sketch, "E4.50.0", {"start": v(11.33, -80.23) * mm, "mid": v(10.5, -79.79) * mm, "end": v(9.82, -80.43) * mm});
            skArc(sketch, "E4.50.1", {"start": v(14.64, -83.08) * mm, "mid": v(14.99, -81.36) * mm, "end": v(15.06, -79.62) * mm});
            skArc(sketch, "E4.50.2", {"start": v(12.84, -83.37) * mm, "mid": v(11.96, -81.86) * mm, "end": v(11.33, -80.23) * mm});
            skArc(sketch, "E4.50.3", {"start": v(12.84, -83.37) * mm, "mid": v(13.84, -83.8) * mm, "end": v(14.64, -83.08) * mm});
            skArc(sketch, "E4.51.0", {"start": v(16.56, -79.32) * mm, "mid": v(15.7, -78.93) * mm, "end": v(15.06, -79.62) * mm});
            skArc(sketch, "E4.51.1", {"start": v(20.04, -81.94) * mm, "mid": v(20.28, -80.2) * mm, "end": v(20.23, -78.46) * mm});
            skArc(sketch, "E4.51.2", {"start": v(18.27, -82.35) * mm, "mid": v(17.29, -80.9) * mm, "end": v(16.56, -79.32) * mm});
            skArc(sketch, "E4.51.3", {"start": v(18.27, -82.35) * mm, "mid": v(19.29, -82.72) * mm, "end": v(20.04, -81.94) * mm});
            skArc(sketch, "E4.52.0", {"start": v(21.7, -78.07) * mm, "mid": v(20.83, -77.73) * mm, "end": v(20.23, -78.46) * mm});
            skArc(sketch, "E4.52.1", {"start": v(25.35, -80.45) * mm, "mid": v(25.48, -78.71) * mm, "end": v(25.32, -76.97) * mm});
            skArc(sketch, "E4.52.2", {"start": v(23.62, -80.98) * mm, "mid": v(22.54, -79.6) * mm, "end": v(21.7, -78.07) * mm});
            skArc(sketch, "E4.52.3", {"start": v(23.62, -80.98) * mm, "mid": v(24.66, -81.28) * mm, "end": v(25.35, -80.45) * mm});
            skArc(sketch, "E4.53.0", {"start": v(26.77, -76.48) * mm, "mid": v(25.87, -76.2) * mm, "end": v(25.32, -76.97) * mm});
            skArc(sketch, "E4.53.1", {"start": v(30.56, -78.62) * mm, "mid": v(30.58, -76.88) * mm, "end": v(30.3, -75.15) * mm});
            skArc(sketch, "E4.53.2", {"start": v(28.86, -79.26) * mm, "mid": v(27.7, -77.96) * mm, "end": v(26.77, -76.48) * mm});
            skArc(sketch, "E4.53.3", {"start": v(28.86, -79.26) * mm, "mid": v(29.92, -79.5) * mm, "end": v(30.56, -78.62) * mm});
            skArc(sketch, "E4.54.0", {"start": v(31.71, -74.56) * mm, "mid": v(30.8, -74.35) * mm, "end": v(30.3, -75.15) * mm});
            skArc(sketch, "E4.54.1", {"start": v(35.64, -76.46) * mm, "mid": v(35.54, -74.71) * mm, "end": v(35.15, -73) * mm});
            skArc(sketch, "E4.54.2", {"start": v(33.99, -77.2) * mm, "mid": v(32.74, -75.98) * mm, "end": v(31.71, -74.56) * mm});
            skArc(sketch, "E4.54.3", {"start": v(33.99, -77.2) * mm, "mid": v(35.05, -77.37) * mm, "end": v(35.64, -76.46) * mm});
            skArc(sketch, "E4.55.0", {"start": v(36.52, -72.33) * mm, "mid": v(35.6, -72.18) * mm, "end": v(35.15, -73) * mm});
            skArc(sketch, "E4.55.1", {"start": v(40.56, -73.96) * mm, "mid": v(40.35, -72.23) * mm, "end": v(39.85, -70.55) * mm});
            skArc(sketch, "E4.55.2", {"start": v(38.96, -74.82) * mm, "mid": v(37.64, -73.68) * mm, "end": v(36.52, -72.33) * mm});
            skArc(sketch, "E4.55.3", {"start": v(38.96, -74.82) * mm, "mid": v(40.04, -74.9) * mm, "end": v(40.56, -73.96) * mm});
            skArc(sketch, "E4.56.0", {"start": v(41.17, -69.79) * mm, "mid": v(40.24, -69.7) * mm, "end": v(39.85, -70.55) * mm});
            skArc(sketch, "E4.56.1", {"start": v(45.31, -71.15) * mm, "mid": v(44.99, -69.43) * mm, "end": v(44.38, -67.8) * mm});
            skArc(sketch, "E4.56.2", {"start": v(43.77, -72.1) * mm, "mid": v(42.38, -71.06) * mm, "end": v(41.17, -69.79) * mm});
            skArc(sketch, "E4.56.3", {"start": v(43.77, -72.1) * mm, "mid": v(44.85, -72.13) * mm, "end": v(45.31, -71.15) * mm});
            skArc(sketch, "E4.57.0", {"start": v(45.65, -66.94) * mm, "mid": v(44.7, -66.91) * mm, "end": v(44.38, -67.8) * mm});
            skArc(sketch, "E4.57.1", {"start": v(49.87, -68.04) * mm, "mid": v(49.43, -66.34) * mm, "end": v(48.72, -64.75) * mm});
            skArc(sketch, "E4.57.2", {"start": v(48.4, -69.1) * mm, "mid": v(46.93, -68.13) * mm, "end": v(45.65, -66.94) * mm});
            skArc(sketch, "E4.57.3", {"start": v(48.4, -69.1) * mm, "mid": v(49.47, -69.04) * mm, "end": v(49.87, -68.04) * mm});
            skArc(sketch, "E4.58.0", {"start": v(49.93, -63.82) * mm, "mid": v(49, -63.85) * mm, "end": v(48.72, -64.75) * mm});
            skArc(sketch, "E4.58.1", {"start": v(54.21, -64.63) * mm, "mid": v(53.66, -62.97) * mm, "end": v(52.85, -61.42) * mm});
            skArc(sketch, "E4.58.2", {"start": v(52.8, -65.78) * mm, "mid": v(51.29, -64.92) * mm, "end": v(49.93, -63.82) * mm});
            skArc(sketch, "E4.58.3", {"start": v(52.8, -65.78) * mm, "mid": v(53.88, -65.66) * mm, "end": v(54.21, -64.63) * mm});
            skArc(sketch, "E4.59.0", {"start": v(54, -60.41) * mm, "mid": v(53.06, -60.5) * mm, "end": v(52.85, -61.42) * mm});
            skArc(sketch, "E4.59.1", {"start": v(58.32, -60.94) * mm, "mid": v(57.67, -59.32) * mm, "end": v(56.75, -57.83) * mm});
            skArc(sketch, "E4.59.2", {"start": v(57, -62.18) * mm, "mid": v(55.43, -61.42) * mm, "end": v(54, -60.41) * mm});
            skArc(sketch, "E4.59.3", {"start": v(57, -62.18) * mm, "mid": v(58.06, -62) * mm, "end": v(58.32, -60.94) * mm});
            skArc(sketch, "E4.60.0", {"start": v(57.83, -56.75) * mm, "mid": v(56.9, -56.9) * mm, "end": v(56.75, -57.83) * mm});
            skArc(sketch, "E4.60.1", {"start": v(62.18, -57) * mm, "mid": v(61.42, -55.43) * mm, "end": v(60.41, -54) * mm});
            skArc(sketch, "E4.60.2", {"start": v(60.94, -58.32) * mm, "mid": v(59.32, -57.67) * mm, "end": v(57.83, -56.75) * mm});
            skArc(sketch, "E4.60.3", {"start": v(60.94, -58.32) * mm, "mid": v(62, -58.06) * mm, "end": v(62.18, -57) * mm});
            skArc(sketch, "E4.61.0", {"start": v(61.42, -52.85) * mm, "mid": v(60.5, -53.06) * mm, "end": v(60.41, -54) * mm});
            skArc(sketch, "E4.61.1", {"start": v(65.78, -52.8) * mm, "mid": v(64.92, -51.29) * mm, "end": v(63.82, -49.93) * mm});
            skArc(sketch, "E4.61.2", {"start": v(64.63, -54.21) * mm, "mid": v(62.97, -53.66) * mm, "end": v(61.42, -52.85) * mm});
            skArc(sketch, "E4.61.3", {"start": v(64.63, -54.21) * mm, "mid": v(65.66, -53.88) * mm, "end": v(65.78, -52.8) * mm});
            skArc(sketch, "E4.62.0", {"start": v(64.75, -48.72) * mm, "mid": v(63.85, -49) * mm, "end": v(63.82, -49.93) * mm});
            skArc(sketch, "E4.62.1", {"start": v(69.1, -48.4) * mm, "mid": v(68.13, -46.93) * mm, "end": v(66.94, -45.65) * mm});
            skArc(sketch, "E4.62.2", {"start": v(68.04, -49.87) * mm, "mid": v(66.34, -49.43) * mm, "end": v(64.75, -48.72) * mm});
            skArc(sketch, "E4.62.3", {"start": v(68.04, -49.87) * mm, "mid": v(69.04, -49.47) * mm, "end": v(69.1, -48.4) * mm});
            skArc(sketch, "E4.63.0", {"start": v(67.8, -44.38) * mm, "mid": v(66.91, -44.7) * mm, "end": v(66.94, -45.65) * mm});
            skArc(sketch, "E4.63.1", {"start": v(72.1, -43.77) * mm, "mid": v(71.06, -42.38) * mm, "end": v(69.79, -41.17) * mm});
            skArc(sketch, "E4.63.2", {"start": v(71.15, -45.31) * mm, "mid": v(69.43, -44.99) * mm, "end": v(67.8, -44.38) * mm});
            skArc(sketch, "E4.63.3", {"start": v(71.15, -45.31) * mm, "mid": v(72.13, -44.85) * mm, "end": v(72.1, -43.77) * mm});
            skArc(sketch, "E4.64.0", {"start": v(70.55, -39.85) * mm, "mid": v(69.7, -40.24) * mm, "end": v(69.79, -41.17) * mm});
            skArc(sketch, "E4.64.1", {"start": v(74.82, -38.96) * mm, "mid": v(73.68, -37.64) * mm, "end": v(72.33, -36.52) * mm});
            skArc(sketch, "E4.64.2", {"start": v(73.96, -40.56) * mm, "mid": v(72.23, -40.35) * mm, "end": v(70.55, -39.85) * mm});
            skArc(sketch, "E4.64.3", {"start": v(73.96, -40.56) * mm, "mid": v(74.9, -40.04) * mm, "end": v(74.82, -38.96) * mm});
            skArc(sketch, "E4.65.0", {"start": v(73, -35.15) * mm, "mid": v(72.18, -35.6) * mm, "end": v(72.33, -36.52) * mm});
            skArc(sketch, "E4.65.1", {"start": v(77.2, -33.99) * mm, "mid": v(75.98, -32.74) * mm, "end": v(74.56, -31.71) * mm});
            skArc(sketch, "E4.65.2", {"start": v(76.46, -35.64) * mm, "mid": v(74.71, -35.54) * mm, "end": v(73, -35.15) * mm});
            skArc(sketch, "E4.65.3", {"start": v(76.46, -35.64) * mm, "mid": v(77.37, -35.05) * mm, "end": v(77.2, -33.99) * mm});
            skArc(sketch, "E4.66.0", {"start": v(75.15, -30.3) * mm, "mid": v(74.35, -30.8) * mm, "end": v(74.56, -31.71) * mm});
            skArc(sketch, "E4.66.1", {"start": v(79.26, -28.86) * mm, "mid": v(77.96, -27.7) * mm, "end": v(76.48, -26.77) * mm});
            skArc(sketch, "E4.66.2", {"start": v(78.62, -30.56) * mm, "mid": v(76.88, -30.58) * mm, "end": v(75.15, -30.3) * mm});
            skArc(sketch, "E4.66.3", {"start": v(78.62, -30.56) * mm, "mid": v(79.5, -29.92) * mm, "end": v(79.26, -28.86) * mm});
            skArc(sketch, "E4.67.0", {"start": v(76.97, -25.32) * mm, "mid": v(76.2, -25.87) * mm, "end": v(76.48, -26.77) * mm});
            skArc(sketch, "E4.67.1", {"start": v(80.98, -23.62) * mm, "mid": v(79.6, -22.54) * mm, "end": v(78.07, -21.7) * mm});
            skArc(sketch, "E4.67.2", {"start": v(80.45, -25.35) * mm, "mid": v(78.71, -25.48) * mm, "end": v(76.97, -25.32) * mm});
            skArc(sketch, "E4.67.3", {"start": v(80.45, -25.35) * mm, "mid": v(81.28, -24.66) * mm, "end": v(80.98, -23.62) * mm});
            skArc(sketch, "E4.68.0", {"start": v(78.46, -20.23) * mm, "mid": v(77.73, -20.83) * mm, "end": v(78.07, -21.7) * mm});
            skArc(sketch, "E4.68.1", {"start": v(82.35, -18.27) * mm, "mid": v(80.9, -17.29) * mm, "end": v(79.32, -16.56) * mm});
            skArc(sketch, "E4.68.2", {"start": v(81.94, -20.04) * mm, "mid": v(80.2, -20.28) * mm, "end": v(78.46, -20.23) * mm});
            skArc(sketch, "E4.68.3", {"start": v(81.94, -20.04) * mm, "mid": v(82.72, -19.29) * mm, "end": v(82.35, -18.27) * mm});
            skArc(sketch, "E4.69.0", {"start": v(79.62, -15.06) * mm, "mid": v(78.93, -15.7) * mm, "end": v(79.32, -16.56) * mm});
            skArc(sketch, "E4.69.1", {"start": v(83.37, -12.84) * mm, "mid": v(81.86, -11.96) * mm, "end": v(80.23, -11.33) * mm});
            skArc(sketch, "E4.69.2", {"start": v(83.08, -14.64) * mm, "mid": v(81.36, -14.99) * mm, "end": v(79.62, -15.06) * mm});
            skArc(sketch, "E4.69.3", {"start": v(83.08, -14.64) * mm, "mid": v(83.8, -13.84) * mm, "end": v(83.37, -12.84) * mm});
            skArc(sketch, "E4.70.0", {"start": v(80.43, -9.82) * mm, "mid": v(79.79, -10.5) * mm, "end": v(80.23, -11.33) * mm});
            skArc(sketch, "E4.70.1", {"start": v(84.03, -7.36) * mm, "mid": v(82.47, -6.58) * mm, "end": v(80.8, -6.06) * mm});
            skArc(sketch, "E4.70.2", {"start": v(83.85, -9.17) * mm, "mid": v(82.17, -9.64) * mm, "end": v(80.43, -9.82) * mm});
            skArc(sketch, "E4.70.3", {"start": v(83.85, -9.17) * mm, "mid": v(84.53, -8.33) * mm, "end": v(84.03, -7.36) * mm});
            skArc(sketch, "E4.71.0", {"start": v(80.9, -4.54) * mm, "mid": v(80.3, -5.26) * mm, "end": v(80.8, -6.06) * mm});
            skArc(sketch, "E4.71.1", {"start": v(84.33, -1.85) * mm, "mid": v(82.72, -1.17) * mm, "end": v(81.02, -0.76) * mm});
            skArc(sketch, "E4.71.2", {"start": v(84.28, -3.67) * mm, "mid": v(82.62, -4.24) * mm, "end": v(80.9, -4.54) * mm});
            skArc(sketch, "E4.71.3", {"start": v(84.28, -3.67) * mm, "mid": v(84.9, -2.78) * mm, "end": v(84.33, -1.85) * mm});
            skArc(sketch, "E4.72.0", {"start": v(81.02, 0.76) * mm, "mid": v(80.48, 0) * mm, "end": v(81.02, -0.76) * mm});
            skArc(sketch, "E4.72.1", {"start": v(84.28, 3.67) * mm, "mid": v(82.62, 4.24) * mm, "end": v(80.9, 4.54) * mm});
            skArc(sketch, "E4.72.2", {"start": v(84.33, 1.85) * mm, "mid": v(82.72, 1.17) * mm, "end": v(81.02, 0.76) * mm});
            skArc(sketch, "E4.72.3", {"start": v(84.33, 1.85) * mm, "mid": v(84.9, 2.78) * mm, "end": v(84.28, 3.67) * mm});
            skArc(sketch, "E4.73.0", {"start": v(80.8, 6.06) * mm, "mid": v(80.3, 5.26) * mm, "end": v(80.9, 4.54) * mm});
            skArc(sketch, "E4.73.1", {"start": v(83.85, 9.17) * mm, "mid": v(82.17, 9.64) * mm, "end": v(80.43, 9.82) * mm});
            skArc(sketch, "E4.73.2", {"start": v(84.03, 7.36) * mm, "mid": v(82.47, 6.58) * mm, "end": v(80.8, 6.06) * mm});
            skArc(sketch, "E4.73.3", {"start": v(84.03, 7.36) * mm, "mid": v(84.53, 8.33) * mm, "end": v(83.85, 9.17) * mm});
            skArc(sketch, "E4.74.0", {"start": v(80.23, 11.33) * mm, "mid": v(79.79, 10.5) * mm, "end": v(80.43, 9.82) * mm});
            skArc(sketch, "E4.74.1", {"start": v(83.08, 14.64) * mm, "mid": v(81.36, 14.99) * mm, "end": v(79.62, 15.06) * mm});
            skArc(sketch, "E4.74.2", {"start": v(83.37, 12.84) * mm, "mid": v(81.86, 11.96) * mm, "end": v(80.23, 11.33) * mm});
            skArc(sketch, "E4.74.3", {"start": v(83.37, 12.84) * mm, "mid": v(83.8, 13.84) * mm, "end": v(83.08, 14.64) * mm});
            skArc(sketch, "E4.75.0", {"start": v(79.32, 16.56) * mm, "mid": v(78.93, 15.7) * mm, "end": v(79.62, 15.06) * mm});
            skArc(sketch, "E4.75.1", {"start": v(81.94, 20.04) * mm, "mid": v(80.2, 20.28) * mm, "end": v(78.46, 20.23) * mm});
            skArc(sketch, "E4.75.2", {"start": v(82.35, 18.27) * mm, "mid": v(80.9, 17.29) * mm, "end": v(79.32, 16.56) * mm});
            skArc(sketch, "E4.75.3", {"start": v(82.35, 18.27) * mm, "mid": v(82.72, 19.29) * mm, "end": v(81.94, 20.04) * mm});
            skArc(sketch, "E4.76.0", {"start": v(78.07, 21.7) * mm, "mid": v(77.73, 20.83) * mm, "end": v(78.46, 20.23) * mm});
            skArc(sketch, "E4.76.1", {"start": v(80.45, 25.35) * mm, "mid": v(78.71, 25.48) * mm, "end": v(76.97, 25.32) * mm});
            skArc(sketch, "E4.76.2", {"start": v(80.98, 23.62) * mm, "mid": v(79.6, 22.54) * mm, "end": v(78.07, 21.7) * mm});
            skArc(sketch, "E4.76.3", {"start": v(80.98, 23.62) * mm, "mid": v(81.28, 24.66) * mm, "end": v(80.45, 25.35) * mm});
            skArc(sketch, "E4.77.0", {"start": v(76.48, 26.77) * mm, "mid": v(76.2, 25.87) * mm, "end": v(76.97, 25.32) * mm});
            skArc(sketch, "E4.77.1", {"start": v(78.62, 30.56) * mm, "mid": v(76.88, 30.58) * mm, "end": v(75.15, 30.3) * mm});
            skArc(sketch, "E4.77.2", {"start": v(79.26, 28.86) * mm, "mid": v(77.96, 27.7) * mm, "end": v(76.48, 26.77) * mm});
            skArc(sketch, "E4.77.3", {"start": v(79.26, 28.86) * mm, "mid": v(79.5, 29.92) * mm, "end": v(78.62, 30.56) * mm});
            skArc(sketch, "E4.78.0", {"start": v(74.56, 31.71) * mm, "mid": v(74.35, 30.8) * mm, "end": v(75.15, 30.3) * mm});
            skArc(sketch, "E4.78.1", {"start": v(76.46, 35.64) * mm, "mid": v(74.71, 35.54) * mm, "end": v(73, 35.15) * mm});
            skArc(sketch, "E4.78.2", {"start": v(77.2, 33.99) * mm, "mid": v(75.98, 32.74) * mm, "end": v(74.56, 31.71) * mm});
            skArc(sketch, "E4.78.3", {"start": v(77.2, 33.99) * mm, "mid": v(77.37, 35.05) * mm, "end": v(76.46, 35.64) * mm});
            skArc(sketch, "E4.79.0", {"start": v(72.33, 36.52) * mm, "mid": v(72.18, 35.6) * mm, "end": v(73, 35.15) * mm});
            skArc(sketch, "E4.79.1", {"start": v(73.96, 40.56) * mm, "mid": v(72.23, 40.35) * mm, "end": v(70.55, 39.85) * mm});
            skArc(sketch, "E4.79.2", {"start": v(74.82, 38.96) * mm, "mid": v(73.68, 37.64) * mm, "end": v(72.33, 36.52) * mm});
            skArc(sketch, "E4.79.3", {"start": v(74.82, 38.96) * mm, "mid": v(74.9, 40.04) * mm, "end": v(73.96, 40.56) * mm});
            skArc(sketch, "E4.80.0", {"start": v(69.79, 41.17) * mm, "mid": v(69.7, 40.24) * mm, "end": v(70.55, 39.85) * mm});
            skArc(sketch, "E4.80.1", {"start": v(71.15, 45.31) * mm, "mid": v(69.43, 44.99) * mm, "end": v(67.8, 44.38) * mm});
            skArc(sketch, "E4.80.2", {"start": v(72.1, 43.77) * mm, "mid": v(71.06, 42.38) * mm, "end": v(69.79, 41.17) * mm});
            skArc(sketch, "E4.80.3", {"start": v(72.1, 43.77) * mm, "mid": v(72.13, 44.85) * mm, "end": v(71.15, 45.31) * mm});
            skArc(sketch, "E4.81.0", {"start": v(66.94, 45.65) * mm, "mid": v(66.91, 44.7) * mm, "end": v(67.8, 44.38) * mm});
            skArc(sketch, "E4.81.1", {"start": v(68.04, 49.87) * mm, "mid": v(66.34, 49.43) * mm, "end": v(64.75, 48.72) * mm});
            skArc(sketch, "E4.81.2", {"start": v(69.1, 48.4) * mm, "mid": v(68.13, 46.93) * mm, "end": v(66.94, 45.65) * mm});
            skArc(sketch, "E4.81.3", {"start": v(69.1, 48.4) * mm, "mid": v(69.04, 49.47) * mm, "end": v(68.04, 49.87) * mm});
            skArc(sketch, "E4.82.0", {"start": v(63.82, 49.93) * mm, "mid": v(63.85, 49) * mm, "end": v(64.75, 48.72) * mm});
            skArc(sketch, "E4.82.1", {"start": v(64.63, 54.21) * mm, "mid": v(62.97, 53.66) * mm, "end": v(61.42, 52.85) * mm});
            skArc(sketch, "E4.82.2", {"start": v(65.78, 52.8) * mm, "mid": v(64.92, 51.29) * mm, "end": v(63.82, 49.93) * mm});
            skArc(sketch, "E4.82.3", {"start": v(65.78, 52.8) * mm, "mid": v(65.66, 53.88) * mm, "end": v(64.63, 54.21) * mm});
            skArc(sketch, "E4.83.0", {"start": v(60.41, 54) * mm, "mid": v(60.5, 53.06) * mm, "end": v(61.42, 52.85) * mm});
            skArc(sketch, "E4.83.1", {"start": v(60.94, 58.32) * mm, "mid": v(59.32, 57.67) * mm, "end": v(57.83, 56.75) * mm});
            skArc(sketch, "E4.83.2", {"start": v(62.18, 57) * mm, "mid": v(61.42, 55.43) * mm, "end": v(60.41, 54) * mm});
            skArc(sketch, "E4.83.3", {"start": v(62.18, 57) * mm, "mid": v(62, 58.06) * mm, "end": v(60.94, 58.32) * mm});
            skArc(sketch, "E4.84.0", {"start": v(56.75, 57.83) * mm, "mid": v(56.9, 56.9) * mm, "end": v(57.83, 56.75) * mm});
            skArc(sketch, "E4.84.1", {"start": v(57, 62.18) * mm, "mid": v(55.43, 61.42) * mm, "end": v(54, 60.41) * mm});
            skArc(sketch, "E4.84.2", {"start": v(58.32, 60.94) * mm, "mid": v(57.67, 59.32) * mm, "end": v(56.75, 57.83) * mm});
            skArc(sketch, "E4.84.3", {"start": v(58.32, 60.94) * mm, "mid": v(58.06, 62) * mm, "end": v(57, 62.18) * mm});
            skArc(sketch, "E4.85.0", {"start": v(52.85, 61.42) * mm, "mid": v(53.06, 60.5) * mm, "end": v(54, 60.41) * mm});
            skArc(sketch, "E4.85.1", {"start": v(52.8, 65.78) * mm, "mid": v(51.29, 64.92) * mm, "end": v(49.93, 63.82) * mm});
            skArc(sketch, "E4.85.2", {"start": v(54.21, 64.63) * mm, "mid": v(53.66, 62.97) * mm, "end": v(52.85, 61.42) * mm});
            skArc(sketch, "E4.85.3", {"start": v(54.21, 64.63) * mm, "mid": v(53.88, 65.66) * mm, "end": v(52.8, 65.78) * mm});
            skArc(sketch, "E4.86.0", {"start": v(48.72, 64.75) * mm, "mid": v(49, 63.85) * mm, "end": v(49.93, 63.82) * mm});
            skArc(sketch, "E4.86.1", {"start": v(48.4, 69.1) * mm, "mid": v(46.93, 68.13) * mm, "end": v(45.65, 66.94) * mm});
            skArc(sketch, "E4.86.2", {"start": v(49.87, 68.04) * mm, "mid": v(49.43, 66.34) * mm, "end": v(48.72, 64.75) * mm});
            skArc(sketch, "E4.86.3", {"start": v(49.87, 68.04) * mm, "mid": v(49.47, 69.04) * mm, "end": v(48.4, 69.1) * mm});
            skArc(sketch, "E4.87.0", {"start": v(44.38, 67.8) * mm, "mid": v(44.7, 66.91) * mm, "end": v(45.65, 66.94) * mm});
            skArc(sketch, "E4.87.1", {"start": v(43.77, 72.1) * mm, "mid": v(42.38, 71.06) * mm, "end": v(41.17, 69.79) * mm});
            skArc(sketch, "E4.87.2", {"start": v(45.31, 71.15) * mm, "mid": v(44.99, 69.43) * mm, "end": v(44.38, 67.8) * mm});
            skArc(sketch, "E4.87.3", {"start": v(45.31, 71.15) * mm, "mid": v(44.85, 72.13) * mm, "end": v(43.77, 72.1) * mm});
            skArc(sketch, "E4.88.0", {"start": v(39.85, 70.55) * mm, "mid": v(40.24, 69.7) * mm, "end": v(41.17, 69.79) * mm});
            skArc(sketch, "E4.88.1", {"start": v(38.96, 74.82) * mm, "mid": v(37.64, 73.68) * mm, "end": v(36.52, 72.33) * mm});
            skArc(sketch, "E4.88.2", {"start": v(40.56, 73.96) * mm, "mid": v(40.35, 72.23) * mm, "end": v(39.85, 70.55) * mm});
            skArc(sketch, "E4.88.3", {"start": v(40.56, 73.96) * mm, "mid": v(40.04, 74.9) * mm, "end": v(38.96, 74.82) * mm});
            skArc(sketch, "E4.89.0", {"start": v(35.15, 73) * mm, "mid": v(35.6, 72.18) * mm, "end": v(36.52, 72.33) * mm});
            skArc(sketch, "E4.89.1", {"start": v(33.99, 77.2) * mm, "mid": v(32.74, 75.98) * mm, "end": v(31.71, 74.56) * mm});
            skArc(sketch, "E4.89.2", {"start": v(35.64, 76.46) * mm, "mid": v(35.54, 74.71) * mm, "end": v(35.15, 73) * mm});
            skArc(sketch, "E4.89.3", {"start": v(35.64, 76.46) * mm, "mid": v(35.05, 77.37) * mm, "end": v(33.99, 77.2) * mm});
            skArc(sketch, "E4.90.0", {"start": v(30.3, 75.15) * mm, "mid": v(30.8, 74.35) * mm, "end": v(31.71, 74.56) * mm});
            skArc(sketch, "E4.90.1", {"start": v(28.86, 79.26) * mm, "mid": v(27.7, 77.96) * mm, "end": v(26.77, 76.48) * mm});
            skArc(sketch, "E4.90.2", {"start": v(30.56, 78.62) * mm, "mid": v(30.58, 76.88) * mm, "end": v(30.3, 75.15) * mm});
            skArc(sketch, "E4.90.3", {"start": v(30.56, 78.62) * mm, "mid": v(29.92, 79.5) * mm, "end": v(28.86, 79.26) * mm});
            skArc(sketch, "E4.91.0", {"start": v(25.32, 76.97) * mm, "mid": v(25.87, 76.2) * mm, "end": v(26.77, 76.48) * mm});
            skArc(sketch, "E4.91.1", {"start": v(23.62, 80.98) * mm, "mid": v(22.54, 79.6) * mm, "end": v(21.7, 78.07) * mm});
            skArc(sketch, "E4.91.2", {"start": v(25.35, 80.45) * mm, "mid": v(25.48, 78.71) * mm, "end": v(25.32, 76.97) * mm});
            skArc(sketch, "E4.91.3", {"start": v(25.35, 80.45) * mm, "mid": v(24.66, 81.28) * mm, "end": v(23.62, 80.98) * mm});
            skArc(sketch, "E4.92.0", {"start": v(20.23, 78.46) * mm, "mid": v(20.83, 77.73) * mm, "end": v(21.7, 78.07) * mm});
            skArc(sketch, "E4.92.1", {"start": v(18.27, 82.35) * mm, "mid": v(17.29, 80.9) * mm, "end": v(16.56, 79.32) * mm});
            skArc(sketch, "E4.92.2", {"start": v(20.04, 81.94) * mm, "mid": v(20.28, 80.2) * mm, "end": v(20.23, 78.46) * mm});
            skArc(sketch, "E4.92.3", {"start": v(20.04, 81.94) * mm, "mid": v(19.29, 82.72) * mm, "end": v(18.27, 82.35) * mm});
            skArc(sketch, "E4.93.0", {"start": v(15.06, 79.62) * mm, "mid": v(15.7, 78.93) * mm, "end": v(16.56, 79.32) * mm});
            skArc(sketch, "E4.93.1", {"start": v(12.84, 83.37) * mm, "mid": v(11.96, 81.86) * mm, "end": v(11.33, 80.23) * mm});
            skArc(sketch, "E4.93.2", {"start": v(14.64, 83.08) * mm, "mid": v(14.99, 81.36) * mm, "end": v(15.06, 79.62) * mm});
            skArc(sketch, "E4.93.3", {"start": v(14.64, 83.08) * mm, "mid": v(13.84, 83.8) * mm, "end": v(12.84, 83.37) * mm});
            skArc(sketch, "E4.94.0", {"start": v(9.82, 80.43) * mm, "mid": v(10.5, 79.79) * mm, "end": v(11.33, 80.23) * mm});
            skArc(sketch, "E4.94.1", {"start": v(7.36, 84.03) * mm, "mid": v(6.58, 82.47) * mm, "end": v(6.06, 80.8) * mm});
            skArc(sketch, "E4.94.2", {"start": v(9.17, 83.85) * mm, "mid": v(9.64, 82.17) * mm, "end": v(9.82, 80.43) * mm});
            skArc(sketch, "E4.94.3", {"start": v(9.17, 83.85) * mm, "mid": v(8.33, 84.53) * mm, "end": v(7.36, 84.03) * mm});
            skArc(sketch, "E4.95.0", {"start": v(4.54, 80.9) * mm, "mid": v(5.26, 80.3) * mm, "end": v(6.06, 80.8) * mm});
            skArc(sketch, "E4.95.1", {"start": v(1.85, 84.33) * mm, "mid": v(1.17, 82.72) * mm, "end": v(0.76, 81.02) * mm});
            skArc(sketch, "E4.95.2", {"start": v(3.67, 84.28) * mm, "mid": v(4.24, 82.62) * mm, "end": v(4.54, 80.9) * mm});
            skArc(sketch, "E4.95.3", {"start": v(3.67, 84.28) * mm, "mid": v(2.78, 84.9) * mm, "end": v(1.85, 84.33) * mm});
            skPoint(sketch, "E4.center", {"position": v(0, 0) * mm});
            skCircle(sketch, "E5", {"center": v(0, 0) * mm, "radius": 95 * mm});
            skSolve(sketch);
        }
        {
            var Q0;
            Q0=makeQuery(id+"F0.imprint","IMPRINT",FACE,{"disambiguationData":[TD([[makeQuery(id+"F0.imprint","IMPRINT",EDGE,{"derivedFrom":sQuery(id+"F0.wireOp",EDGE,"E0.1.2")}),-1.0]])]});
            extrude(context, id + "F1", {"entities" : qUnion([Q0]), "depth" : 5 * mm});
        }
        {
            var Q0;
            Q0=makeQuery(id+"F1.opExtrude","CAP_FACE",FACE,{"disambiguationData":[OSD([sQuery(id+"F0.wireOp",EDGE,"E0.1.2"),sQuery(id+"F0.wireOp",EDGE,"E1.MirrorCS"),sQuery(id+"F0.wireOp",EDGE,"E2"),sQuery(id+"F0.wireOp",EDGE,"E3"),sQuery(id+"F0.wireOp",EDGE,"E4.1.0"),sQuery(id+"F0.wireOp",EDGE,"E4.1.1"),sQuery(id+"F0.wireOp",EDGE,"E4.1.2"),sQuery(id+"F0.wireOp",EDGE,"E4.1.3"),sQuery(id+"F0.wireOp",EDGE,"E4.2.0"),sQuery(id+"F0.wireOp",EDGE,"E4.2.1"),sQuery(id+"F0.wireOp",EDGE,"E4.2.2"),sQuery(id+"F0.wireOp",EDGE,"E4.2.3"),sQuery(id+"F0.wireOp",EDGE,"E4.3.0"),sQuery(id+"F0.wireOp",EDGE,"E4.3.1"),sQuery(id+"F0.wireOp",EDGE,"E4.3.2"),sQuery(id+"F0.wireOp",EDGE,"E4.3.3"),sQuery(id+"F0.wireOp",EDGE,"E4.4.0"),sQuery(id+"F0.wireOp",EDGE,"E4.4.1"),sQuery(id+"F0.wireOp",EDGE,"E4.4.2"),sQuery(id+"F0.wireOp",EDGE,"E4.4.3"),sQuery(id+"F0.wireOp",EDGE,"E4.5.0"),sQuery(id+"F0.wireOp",EDGE,"E4.5.1"),sQuery(id+"F0.wireOp",EDGE,"E4.5.2"),sQuery(id+"F0.wireOp",EDGE,"E4.5.3"),sQuery(id+"F0.wireOp",EDGE,"E4.6.0"),sQuery(id+"F0.wireOp",EDGE,"E4.6.1"),sQuery(id+"F0.wireOp",EDGE,"E4.6.2"),sQuery(id+"F0.wireOp",EDGE,"E4.6.3"),sQuery(id+"F0.wireOp",EDGE,"E4.7.0"),sQuery(id+"F0.wireOp",EDGE,"E4.7.1"),sQuery(id+"F0.wireOp",EDGE,"E4.7.2"),sQuery(id+"F0.wireOp",EDGE,"E4.7.3"),sQuery(id+"F0.wireOp",EDGE,"E4.8.0"),sQuery(id+"F0.wireOp",EDGE,"E4.8.1"),sQuery(id+"F0.wireOp",EDGE,"E4.8.2"),sQuery(id+"F0.wireOp",EDGE,"E4.8.3"),sQuery(id+"F0.wireOp",EDGE,"E4.9.0"),sQuery(id+"F0.wireOp",EDGE,"E4.9.1"),sQuery(id+"F0.wireOp",EDGE,"E4.9.2"),sQuery(id+"F0.wireOp",EDGE,"E4.9.3"),sQuery(id+"F0.wireOp",EDGE,"E4.10.0"),sQuery(id+"F0.wireOp",EDGE,"E4.10.1"),sQuery(id+"F0.wireOp",EDGE,"E4.10.2"),sQuery(id+"F0.wireOp",EDGE,"E4.10.3"),sQuery(id+"F0.wireOp",EDGE,"E4.11.0"),sQuery(id+"F0.wireOp",EDGE,"E4.11.1"),sQuery(id+"F0.wireOp",EDGE,"E4.11.2"),sQuery(id+"F0.wireOp",EDGE,"E4.11.3"),sQuery(id+"F0.wireOp",EDGE,"E4.12.0"),sQuery(id+"F0.wireOp",EDGE,"E4.12.1"),sQuery(id+"F0.wireOp",EDGE,"E4.12.2"),sQuery(id+"F0.wireOp",EDGE,"E4.12.3"),sQuery(id+"F0.wireOp",EDGE,"E4.13.0"),sQuery(id+"F0.wireOp",EDGE,"E4.13.1"),sQuery(id+"F0.wireOp",EDGE,"E4.13.2"),sQuery(id+"F0.wireOp",EDGE,"E4.13.3"),sQuery(id+"F0.wireOp",EDGE,"E4.14.0"),sQuery(id+"F0.wireOp",EDGE,"E4.14.1"),sQuery(id+"F0.wireOp",EDGE,"E4.14.2"),sQuery(id+"F0.wireOp",EDGE,"E4.14.3"),sQuery(id+"F0.wireOp",EDGE,"E4.15.0"),sQuery(id+"F0.wireOp",EDGE,"E4.15.1"),sQuery(id+"F0.wireOp",EDGE,"E4.15.2"),sQuery(id+"F0.wireOp",EDGE,"E4.15.3"),sQuery(id+"F0.wireOp",EDGE,"E4.16.0"),sQuery(id+"F0.wireOp",EDGE,"E4.16.1"),sQuery(id+"F0.wireOp",EDGE,"E4.16.2"),sQuery(id+"F0.wireOp",EDGE,"E4.16.3"),sQuery(id+"F0.wireOp",EDGE,"E4.17.0"),sQuery(id+"F0.wireOp",EDGE,"E4.17.1"),sQuery(id+"F0.wireOp",EDGE,"E4.17.2"),sQuery(id+"F0.wireOp",EDGE,"E4.17.3"),sQuery(id+"F0.wireOp",EDGE,"E4.18.0"),sQuery(id+"F0.wireOp",EDGE,"E4.18.1"),sQuery(id+"F0.wireOp",EDGE,"E4.18.2"),sQuery(id+"F0.wireOp",EDGE,"E4.18.3"),sQuery(id+"F0.wireOp",EDGE,"E4.19.0"),sQuery(id+"F0.wireOp",EDGE,"E4.19.1"),sQuery(id+"F0.wireOp",EDGE,"E4.19.2"),sQuery(id+"F0.wireOp",EDGE,"E4.19.3"),sQuery(id+"F0.wireOp",EDGE,"E4.20.0"),sQuery(id+"F0.wireOp",EDGE,"E4.20.1"),sQuery(id+"F0.wireOp",EDGE,"E4.20.2"),sQuery(id+"F0.wireOp",EDGE,"E4.20.3"),sQuery(id+"F0.wireOp",EDGE,"E4.21.0"),sQuery(id+"F0.wireOp",EDGE,"E4.21.1"),sQuery(id+"F0.wireOp",EDGE,"E4.21.2"),sQuery(id+"F0.wireOp",EDGE,"E4.21.3"),sQuery(id+"F0.wireOp",EDGE,"E4.22.0"),sQuery(id+"F0.wireOp",EDGE,"E4.22.1"),sQuery(id+"F0.wireOp",EDGE,"E4.22.2"),sQuery(id+"F0.wireOp",EDGE,"E4.22.3"),sQuery(id+"F0.wireOp",EDGE,"E4.23.0"),sQuery(id+"F0.wireOp",EDGE,"E4.23.1"),sQuery(id+"F0.wireOp",EDGE,"E4.23.2"),sQuery(id+"F0.wireOp",EDGE,"E4.23.3"),sQuery(id+"F0.wireOp",EDGE,"E4.24.0"),sQuery(id+"F0.wireOp",EDGE,"E4.24.1"),sQuery(id+"F0.wireOp",EDGE,"E4.24.2"),sQuery(id+"F0.wireOp",EDGE,"E4.24.3"),sQuery(id+"F0.wireOp",EDGE,"E4.25.0"),sQuery(id+"F0.wireOp",EDGE,"E4.25.1"),sQuery(id+"F0.wireOp",EDGE,"E4.25.2"),sQuery(id+"F0.wireOp",EDGE,"E4.25.3"),sQuery(id+"F0.wireOp",EDGE,"E4.26.0"),sQuery(id+"F0.wireOp",EDGE,"E4.26.1"),sQuery(id+"F0.wireOp",EDGE,"E4.26.2"),sQuery(id+"F0.wireOp",EDGE,"E4.26.3"),sQuery(id+"F0.wireOp",EDGE,"E4.27.0"),sQuery(id+"F0.wireOp",EDGE,"E4.27.1"),sQuery(id+"F0.wireOp",EDGE,"E4.27.2"),sQuery(id+"F0.wireOp",EDGE,"E4.27.3"),sQuery(id+"F0.wireOp",EDGE,"E4.28.0"),sQuery(id+"F0.wireOp",EDGE,"E4.28.1"),sQuery(id+"F0.wireOp",EDGE,"E4.28.2"),sQuery(id+"F0.wireOp",EDGE,"E4.28.3"),sQuery(id+"F0.wireOp",EDGE,"E4.29.0"),sQuery(id+"F0.wireOp",EDGE,"E4.29.1"),sQuery(id+"F0.wireOp",EDGE,"E4.29.2"),sQuery(id+"F0.wireOp",EDGE,"E4.29.3"),sQuery(id+"F0.wireOp",EDGE,"E4.30.0"),sQuery(id+"F0.wireOp",EDGE,"E4.30.1"),sQuery(id+"F0.wireOp",EDGE,"E4.30.2"),sQuery(id+"F0.wireOp",EDGE,"E4.30.3"),sQuery(id+"F0.wireOp",EDGE,"E4.31.0"),sQuery(id+"F0.wireOp",EDGE,"E4.31.1"),sQuery(id+"F0.wireOp",EDGE,"E4.31.2"),sQuery(id+"F0.wireOp",EDGE,"E4.31.3"),sQuery(id+"F0.wireOp",EDGE,"E4.32.0"),sQuery(id+"F0.wireOp",EDGE,"E4.32.1"),sQuery(id+"F0.wireOp",EDGE,"E4.32.2"),sQuery(id+"F0.wireOp",EDGE,"E4.32.3"),sQuery(id+"F0.wireOp",EDGE,"E4.33.0"),sQuery(id+"F0.wireOp",EDGE,"E4.33.1"),sQuery(id+"F0.wireOp",EDGE,"E4.33.2"),sQuery(id+"F0.wireOp",EDGE,"E4.33.3"),sQuery(id+"F0.wireOp",EDGE,"E4.34.0"),sQuery(id+"F0.wireOp",EDGE,"E4.34.1"),sQuery(id+"F0.wireOp",EDGE,"E4.34.2"),sQuery(id+"F0.wireOp",EDGE,"E4.34.3"),sQuery(id+"F0.wireOp",EDGE,"E4.35.0"),sQuery(id+"F0.wireOp",EDGE,"E4.35.1"),sQuery(id+"F0.wireOp",EDGE,"E4.35.2"),sQuery(id+"F0.wireOp",EDGE,"E4.35.3"),sQuery(id+"F0.wireOp",EDGE,"E4.36.0"),sQuery(id+"F0.wireOp",EDGE,"E4.36.1"),sQuery(id+"F0.wireOp",EDGE,"E4.36.2"),sQuery(id+"F0.wireOp",EDGE,"E4.36.3"),sQuery(id+"F0.wireOp",EDGE,"E4.37.0"),sQuery(id+"F0.wireOp",EDGE,"E4.37.1"),sQuery(id+"F0.wireOp",EDGE,"E4.37.2"),sQuery(id+"F0.wireOp",EDGE,"E4.37.3"),sQuery(id+"F0.wireOp",EDGE,"E4.38.0"),sQuery(id+"F0.wireOp",EDGE,"E4.38.1"),sQuery(id+"F0.wireOp",EDGE,"E4.38.2"),sQuery(id+"F0.wireOp",EDGE,"E4.38.3"),sQuery(id+"F0.wireOp",EDGE,"E4.39.0"),sQuery(id+"F0.wireOp",EDGE,"E4.39.1"),sQuery(id+"F0.wireOp",EDGE,"E4.39.2"),sQuery(id+"F0.wireOp",EDGE,"E4.39.3"),sQuery(id+"F0.wireOp",EDGE,"E4.40.0"),sQuery(id+"F0.wireOp",EDGE,"E4.40.1"),sQuery(id+"F0.wireOp",EDGE,"E4.40.2"),sQuery(id+"F0.wireOp",EDGE,"E4.40.3"),sQuery(id+"F0.wireOp",EDGE,"E4.41.0"),sQuery(id+"F0.wireOp",EDGE,"E4.41.1"),sQuery(id+"F0.wireOp",EDGE,"E4.41.2"),sQuery(id+"F0.wireOp",EDGE,"E4.41.3"),sQuery(id+"F0.wireOp",EDGE,"E4.42.0"),sQuery(id+"F0.wireOp",EDGE,"E4.42.1"),sQuery(id+"F0.wireOp",EDGE,"E4.42.2"),sQuery(id+"F0.wireOp",EDGE,"E4.42.3"),sQuery(id+"F0.wireOp",EDGE,"E4.43.0"),sQuery(id+"F0.wireOp",EDGE,"E4.43.1"),sQuery(id+"F0.wireOp",EDGE,"E4.43.2"),sQuery(id+"F0.wireOp",EDGE,"E4.43.3"),sQuery(id+"F0.wireOp",EDGE,"E4.44.0"),sQuery(id+"F0.wireOp",EDGE,"E4.44.1"),sQuery(id+"F0.wireOp",EDGE,"E4.44.2"),sQuery(id+"F0.wireOp",EDGE,"E4.44.3"),sQuery(id+"F0.wireOp",EDGE,"E4.45.0"),sQuery(id+"F0.wireOp",EDGE,"E4.45.1"),sQuery(id+"F0.wireOp",EDGE,"E4.45.2"),sQuery(id+"F0.wireOp",EDGE,"E4.45.3"),sQuery(id+"F0.wireOp",EDGE,"E4.46.0"),sQuery(id+"F0.wireOp",EDGE,"E4.46.1"),sQuery(id+"F0.wireOp",EDGE,"E4.46.2"),sQuery(id+"F0.wireOp",EDGE,"E4.46.3"),sQuery(id+"F0.wireOp",EDGE,"E4.47.0"),sQuery(id+"F0.wireOp",EDGE,"E4.47.1"),sQuery(id+"F0.wireOp",EDGE,"E4.47.2"),sQuery(id+"F0.wireOp",EDGE,"E4.47.3"),sQuery(id+"F0.wireOp",EDGE,"E4.48.0"),sQuery(id+"F0.wireOp",EDGE,"E4.48.1"),sQuery(id+"F0.wireOp",EDGE,"E4.48.2"),sQuery(id+"F0.wireOp",EDGE,"E4.48.3"),sQuery(id+"F0.wireOp",EDGE,"E4.49.0"),sQuery(id+"F0.wireOp",EDGE,"E4.49.1"),sQuery(id+"F0.wireOp",EDGE,"E4.49.2"),sQuery(id+"F0.wireOp",EDGE,"E4.49.3"),sQuery(id+"F0.wireOp",EDGE,"E4.50.0"),sQuery(id+"F0.wireOp",EDGE,"E4.50.1"),sQuery(id+"F0.wireOp",EDGE,"E4.50.2"),sQuery(id+"F0.wireOp",EDGE,"E4.50.3"),sQuery(id+"F0.wireOp",EDGE,"E4.51.0"),sQuery(id+"F0.wireOp",EDGE,"E4.51.1"),sQuery(id+"F0.wireOp",EDGE,"E4.51.2"),sQuery(id+"F0.wireOp",EDGE,"E4.51.3"),sQuery(id+"F0.wireOp",EDGE,"E4.52.0"),sQuery(id+"F0.wireOp",EDGE,"E4.52.1"),sQuery(id+"F0.wireOp",EDGE,"E4.52.2"),sQuery(id+"F0.wireOp",EDGE,"E4.52.3"),sQuery(id+"F0.wireOp",EDGE,"E4.53.0"),sQuery(id+"F0.wireOp",EDGE,"E4.53.1"),sQuery(id+"F0.wireOp",EDGE,"E4.53.2"),sQuery(id+"F0.wireOp",EDGE,"E4.53.3"),sQuery(id+"F0.wireOp",EDGE,"E4.54.0"),sQuery(id+"F0.wireOp",EDGE,"E4.54.1"),sQuery(id+"F0.wireOp",EDGE,"E4.54.2"),sQuery(id+"F0.wireOp",EDGE,"E4.54.3"),sQuery(id+"F0.wireOp",EDGE,"E4.55.0"),sQuery(id+"F0.wireOp",EDGE,"E4.55.1"),sQuery(id+"F0.wireOp",EDGE,"E4.55.2"),sQuery(id+"F0.wireOp",EDGE,"E4.55.3"),sQuery(id+"F0.wireOp",EDGE,"E4.56.0"),sQuery(id+"F0.wireOp",EDGE,"E4.56.1"),sQuery(id+"F0.wireOp",EDGE,"E4.56.2"),sQuery(id+"F0.wireOp",EDGE,"E4.56.3"),sQuery(id+"F0.wireOp",EDGE,"E4.57.0"),sQuery(id+"F0.wireOp",EDGE,"E4.57.1"),sQuery(id+"F0.wireOp",EDGE,"E4.57.2"),sQuery(id+"F0.wireOp",EDGE,"E4.57.3"),sQuery(id+"F0.wireOp",EDGE,"E4.58.0"),sQuery(id+"F0.wireOp",EDGE,"E4.58.1"),sQuery(id+"F0.wireOp",EDGE,"E4.58.2"),sQuery(id+"F0.wireOp",EDGE,"E4.58.3"),sQuery(id+"F0.wireOp",EDGE,"E4.59.0"),sQuery(id+"F0.wireOp",EDGE,"E4.59.1"),sQuery(id+"F0.wireOp",EDGE,"E4.59.2"),sQuery(id+"F0.wireOp",EDGE,"E4.59.3"),sQuery(id+"F0.wireOp",EDGE,"E4.60.0"),sQuery(id+"F0.wireOp",EDGE,"E4.60.1"),sQuery(id+"F0.wireOp",EDGE,"E4.60.2"),sQuery(id+"F0.wireOp",EDGE,"E4.60.3"),sQuery(id+"F0.wireOp",EDGE,"E4.61.0"),sQuery(id+"F0.wireOp",EDGE,"E4.61.1"),sQuery(id+"F0.wireOp",EDGE,"E4.61.2"),sQuery(id+"F0.wireOp",EDGE,"E4.61.3"),sQuery(id+"F0.wireOp",EDGE,"E4.62.0"),sQuery(id+"F0.wireOp",EDGE,"E4.62.1"),sQuery(id+"F0.wireOp",EDGE,"E4.62.2"),sQuery(id+"F0.wireOp",EDGE,"E4.62.3"),sQuery(id+"F0.wireOp",EDGE,"E4.63.0"),sQuery(id+"F0.wireOp",EDGE,"E4.63.1"),sQuery(id+"F0.wireOp",EDGE,"E4.63.2"),sQuery(id+"F0.wireOp",EDGE,"E4.63.3"),sQuery(id+"F0.wireOp",EDGE,"E4.64.0"),sQuery(id+"F0.wireOp",EDGE,"E4.64.1"),sQuery(id+"F0.wireOp",EDGE,"E4.64.2"),sQuery(id+"F0.wireOp",EDGE,"E4.64.3"),sQuery(id+"F0.wireOp",EDGE,"E4.65.0"),sQuery(id+"F0.wireOp",EDGE,"E4.65.1"),sQuery(id+"F0.wireOp",EDGE,"E4.65.2"),sQuery(id+"F0.wireOp",EDGE,"E4.65.3"),sQuery(id+"F0.wireOp",EDGE,"E4.66.0"),sQuery(id+"F0.wireOp",EDGE,"E4.66.1"),sQuery(id+"F0.wireOp",EDGE,"E4.66.2"),sQuery(id+"F0.wireOp",EDGE,"E4.66.3"),sQuery(id+"F0.wireOp",EDGE,"E4.67.0"),sQuery(id+"F0.wireOp",EDGE,"E4.67.1"),sQuery(id+"F0.wireOp",EDGE,"E4.67.2"),sQuery(id+"F0.wireOp",EDGE,"E4.67.3"),sQuery(id+"F0.wireOp",EDGE,"E4.68.0"),sQuery(id+"F0.wireOp",EDGE,"E4.68.1"),sQuery(id+"F0.wireOp",EDGE,"E4.68.2"),sQuery(id+"F0.wireOp",EDGE,"E4.68.3"),sQuery(id+"F0.wireOp",EDGE,"E4.69.0"),sQuery(id+"F0.wireOp",EDGE,"E4.69.1"),sQuery(id+"F0.wireOp",EDGE,"E4.69.2"),sQuery(id+"F0.wireOp",EDGE,"E4.69.3"),sQuery(id+"F0.wireOp",EDGE,"E4.70.0"),sQuery(id+"F0.wireOp",EDGE,"E4.70.1"),sQuery(id+"F0.wireOp",EDGE,"E4.70.2"),sQuery(id+"F0.wireOp",EDGE,"E4.70.3"),sQuery(id+"F0.wireOp",EDGE,"E4.71.0"),sQuery(id+"F0.wireOp",EDGE,"E4.71.1"),sQuery(id+"F0.wireOp",EDGE,"E4.71.2"),sQuery(id+"F0.wireOp",EDGE,"E4.71.3"),sQuery(id+"F0.wireOp",EDGE,"E4.72.0"),sQuery(id+"F0.wireOp",EDGE,"E4.72.1"),sQuery(id+"F0.wireOp",EDGE,"E4.72.2"),sQuery(id+"F0.wireOp",EDGE,"E4.72.3"),sQuery(id+"F0.wireOp",EDGE,"E4.73.0"),sQuery(id+"F0.wireOp",EDGE,"E4.73.1"),sQuery(id+"F0.wireOp",EDGE,"E4.73.2"),sQuery(id+"F0.wireOp",EDGE,"E4.73.3"),sQuery(id+"F0.wireOp",EDGE,"E4.74.0"),sQuery(id+"F0.wireOp",EDGE,"E4.74.1"),sQuery(id+"F0.wireOp",EDGE,"E4.74.2"),sQuery(id+"F0.wireOp",EDGE,"E4.74.3"),sQuery(id+"F0.wireOp",EDGE,"E4.75.0"),sQuery(id+"F0.wireOp",EDGE,"E4.75.1"),sQuery(id+"F0.wireOp",EDGE,"E4.75.2"),sQuery(id+"F0.wireOp",EDGE,"E4.75.3"),sQuery(id+"F0.wireOp",EDGE,"E4.76.0"),sQuery(id+"F0.wireOp",EDGE,"E4.76.1"),sQuery(id+"F0.wireOp",EDGE,"E4.76.2"),sQuery(id+"F0.wireOp",EDGE,"E4.76.3"),sQuery(id+"F0.wireOp",EDGE,"E4.77.0"),sQuery(id+"F0.wireOp",EDGE,"E4.77.1"),sQuery(id+"F0.wireOp",EDGE,"E4.77.2"),sQuery(id+"F0.wireOp",EDGE,"E4.77.3"),sQuery(id+"F0.wireOp",EDGE,"E4.78.0"),sQuery(id+"F0.wireOp",EDGE,"E4.78.1"),sQuery(id+"F0.wireOp",EDGE,"E4.78.2"),sQuery(id+"F0.wireOp",EDGE,"E4.78.3"),sQuery(id+"F0.wireOp",EDGE,"E4.79.0"),sQuery(id+"F0.wireOp",EDGE,"E4.79.1"),sQuery(id+"F0.wireOp",EDGE,"E4.79.2"),sQuery(id+"F0.wireOp",EDGE,"E4.79.3"),sQuery(id+"F0.wireOp",EDGE,"E4.80.0"),sQuery(id+"F0.wireOp",EDGE,"E4.80.1"),sQuery(id+"F0.wireOp",EDGE,"E4.80.2"),sQuery(id+"F0.wireOp",EDGE,"E4.80.3"),sQuery(id+"F0.wireOp",EDGE,"E4.81.0"),sQuery(id+"F0.wireOp",EDGE,"E4.81.1"),sQuery(id+"F0.wireOp",EDGE,"E4.81.2"),sQuery(id+"F0.wireOp",EDGE,"E4.81.3"),sQuery(id+"F0.wireOp",EDGE,"E4.82.0"),sQuery(id+"F0.wireOp",EDGE,"E4.82.1"),sQuery(id+"F0.wireOp",EDGE,"E4.82.2"),sQuery(id+"F0.wireOp",EDGE,"E4.82.3"),sQuery(id+"F0.wireOp",EDGE,"E4.83.0"),sQuery(id+"F0.wireOp",EDGE,"E4.83.1"),sQuery(id+"F0.wireOp",EDGE,"E4.83.2"),sQuery(id+"F0.wireOp",EDGE,"E4.83.3"),sQuery(id+"F0.wireOp",EDGE,"E4.84.0"),sQuery(id+"F0.wireOp",EDGE,"E4.84.1"),sQuery(id+"F0.wireOp",EDGE,"E4.84.2"),sQuery(id+"F0.wireOp",EDGE,"E4.84.3"),sQuery(id+"F0.wireOp",EDGE,"E4.85.0"),sQuery(id+"F0.wireOp",EDGE,"E4.85.1"),sQuery(id+"F0.wireOp",EDGE,"E4.85.2"),sQuery(id+"F0.wireOp",EDGE,"E4.85.3"),sQuery(id+"F0.wireOp",EDGE,"E4.86.0"),sQuery(id+"F0.wireOp",EDGE,"E4.86.1"),sQuery(id+"F0.wireOp",EDGE,"E4.86.2"),sQuery(id+"F0.wireOp",EDGE,"E4.86.3"),sQuery(id+"F0.wireOp",EDGE,"E4.87.0"),sQuery(id+"F0.wireOp",EDGE,"E4.87.1"),sQuery(id+"F0.wireOp",EDGE,"E4.87.2"),sQuery(id+"F0.wireOp",EDGE,"E4.87.3"),sQuery(id+"F0.wireOp",EDGE,"E4.88.0"),sQuery(id+"F0.wireOp",EDGE,"E4.88.1"),sQuery(id+"F0.wireOp",EDGE,"E4.88.2"),sQuery(id+"F0.wireOp",EDGE,"E4.88.3"),sQuery(id+"F0.wireOp",EDGE,"E4.89.0"),sQuery(id+"F0.wireOp",EDGE,"E4.89.1"),sQuery(id+"F0.wireOp",EDGE,"E4.89.2"),sQuery(id+"F0.wireOp",EDGE,"E4.89.3"),sQuery(id+"F0.wireOp",EDGE,"E4.90.0"),sQuery(id+"F0.wireOp",EDGE,"E4.90.1"),sQuery(id+"F0.wireOp",EDGE,"E4.90.2"),sQuery(id+"F0.wireOp",EDGE,"E4.90.3"),sQuery(id+"F0.wireOp",EDGE,"E4.91.0"),sQuery(id+"F0.wireOp",EDGE,"E4.91.1"),sQuery(id+"F0.wireOp",EDGE,"E4.91.2"),sQuery(id+"F0.wireOp",EDGE,"E4.91.3"),sQuery(id+"F0.wireOp",EDGE,"E4.92.0"),sQuery(id+"F0.wireOp",EDGE,"E4.92.1"),sQuery(id+"F0.wireOp",EDGE,"E4.92.2"),sQuery(id+"F0.wireOp",EDGE,"E4.92.3"),sQuery(id+"F0.wireOp",EDGE,"E4.93.0"),sQuery(id+"F0.wireOp",EDGE,"E4.93.1"),sQuery(id+"F0.wireOp",EDGE,"E4.93.2"),sQuery(id+"F0.wireOp",EDGE,"E4.93.3"),sQuery(id+"F0.wireOp",EDGE,"E4.94.0"),sQuery(id+"F0.wireOp",EDGE,"E4.94.1"),sQuery(id+"F0.wireOp",EDGE,"E4.94.2"),sQuery(id+"F0.wireOp",EDGE,"E4.94.3"),sQuery(id+"F0.wireOp",EDGE,"E4.95.0"),sQuery(id+"F0.wireOp",EDGE,"E4.95.1"),sQuery(id+"F0.wireOp",EDGE,"E4.95.2"),sQuery(id+"F0.wireOp",EDGE,"E4.95.3"),sQuery(id+"F0.wireOp",EDGE,"E5")])],"isStart":false});
            var Q1;
            Q1=makeQuery(id+"F1.opExtrude","CAP_FACE",FACE,{"disambiguationData":[OSD([sQuery(id+"F0.wireOp",EDGE,"E0.1.2"),sQuery(id+"F0.wireOp",EDGE,"E1.MirrorCS"),sQuery(id+"F0.wireOp",EDGE,"E2"),sQuery(id+"F0.wireOp",EDGE,"E3"),sQuery(id+"F0.wireOp",EDGE,"E4.1.0"),sQuery(id+"F0.wireOp",EDGE,"E4.1.1"),sQuery(id+"F0.wireOp",EDGE,"E4.1.2"),sQuery(id+"F0.wireOp",EDGE,"E4.1.3"),sQuery(id+"F0.wireOp",EDGE,"E4.2.0"),sQuery(id+"F0.wireOp",EDGE,"E4.2.1"),sQuery(id+"F0.wireOp",EDGE,"E4.2.2"),sQuery(id+"F0.wireOp",EDGE,"E4.2.3"),sQuery(id+"F0.wireOp",EDGE,"E4.3.0"),sQuery(id+"F0.wireOp",EDGE,"E4.3.1"),sQuery(id+"F0.wireOp",EDGE,"E4.3.2"),sQuery(id+"F0.wireOp",EDGE,"E4.3.3"),sQuery(id+"F0.wireOp",EDGE,"E4.4.0"),sQuery(id+"F0.wireOp",EDGE,"E4.4.1"),sQuery(id+"F0.wireOp",EDGE,"E4.4.2"),sQuery(id+"F0.wireOp",EDGE,"E4.4.3"),sQuery(id+"F0.wireOp",EDGE,"E4.5.0"),sQuery(id+"F0.wireOp",EDGE,"E4.5.1"),sQuery(id+"F0.wireOp",EDGE,"E4.5.2"),sQuery(id+"F0.wireOp",EDGE,"E4.5.3"),sQuery(id+"F0.wireOp",EDGE,"E4.6.0"),sQuery(id+"F0.wireOp",EDGE,"E4.6.1"),sQuery(id+"F0.wireOp",EDGE,"E4.6.2"),sQuery(id+"F0.wireOp",EDGE,"E4.6.3"),sQuery(id+"F0.wireOp",EDGE,"E4.7.0"),sQuery(id+"F0.wireOp",EDGE,"E4.7.1"),sQuery(id+"F0.wireOp",EDGE,"E4.7.2"),sQuery(id+"F0.wireOp",EDGE,"E4.7.3"),sQuery(id+"F0.wireOp",EDGE,"E4.8.0"),sQuery(id+"F0.wireOp",EDGE,"E4.8.1"),sQuery(id+"F0.wireOp",EDGE,"E4.8.2"),sQuery(id+"F0.wireOp",EDGE,"E4.8.3"),sQuery(id+"F0.wireOp",EDGE,"E4.9.0"),sQuery(id+"F0.wireOp",EDGE,"E4.9.1"),sQuery(id+"F0.wireOp",EDGE,"E4.9.2"),sQuery(id+"F0.wireOp",EDGE,"E4.9.3"),sQuery(id+"F0.wireOp",EDGE,"E4.10.0"),sQuery(id+"F0.wireOp",EDGE,"E4.10.1"),sQuery(id+"F0.wireOp",EDGE,"E4.10.2"),sQuery(id+"F0.wireOp",EDGE,"E4.10.3"),sQuery(id+"F0.wireOp",EDGE,"E4.11.0"),sQuery(id+"F0.wireOp",EDGE,"E4.11.1"),sQuery(id+"F0.wireOp",EDGE,"E4.11.2"),sQuery(id+"F0.wireOp",EDGE,"E4.11.3"),sQuery(id+"F0.wireOp",EDGE,"E4.12.0"),sQuery(id+"F0.wireOp",EDGE,"E4.12.1"),sQuery(id+"F0.wireOp",EDGE,"E4.12.2"),sQuery(id+"F0.wireOp",EDGE,"E4.12.3"),sQuery(id+"F0.wireOp",EDGE,"E4.13.0"),sQuery(id+"F0.wireOp",EDGE,"E4.13.1"),sQuery(id+"F0.wireOp",EDGE,"E4.13.2"),sQuery(id+"F0.wireOp",EDGE,"E4.13.3"),sQuery(id+"F0.wireOp",EDGE,"E4.14.0"),sQuery(id+"F0.wireOp",EDGE,"E4.14.1"),sQuery(id+"F0.wireOp",EDGE,"E4.14.2"),sQuery(id+"F0.wireOp",EDGE,"E4.14.3"),sQuery(id+"F0.wireOp",EDGE,"E4.15.0"),sQuery(id+"F0.wireOp",EDGE,"E4.15.1"),sQuery(id+"F0.wireOp",EDGE,"E4.15.2"),sQuery(id+"F0.wireOp",EDGE,"E4.15.3"),sQuery(id+"F0.wireOp",EDGE,"E4.16.0"),sQuery(id+"F0.wireOp",EDGE,"E4.16.1"),sQuery(id+"F0.wireOp",EDGE,"E4.16.2"),sQuery(id+"F0.wireOp",EDGE,"E4.16.3"),sQuery(id+"F0.wireOp",EDGE,"E4.17.0"),sQuery(id+"F0.wireOp",EDGE,"E4.17.1"),sQuery(id+"F0.wireOp",EDGE,"E4.17.2"),sQuery(id+"F0.wireOp",EDGE,"E4.17.3"),sQuery(id+"F0.wireOp",EDGE,"E4.18.0"),sQuery(id+"F0.wireOp",EDGE,"E4.18.1"),sQuery(id+"F0.wireOp",EDGE,"E4.18.2"),sQuery(id+"F0.wireOp",EDGE,"E4.18.3"),sQuery(id+"F0.wireOp",EDGE,"E4.19.0"),sQuery(id+"F0.wireOp",EDGE,"E4.19.1"),sQuery(id+"F0.wireOp",EDGE,"E4.19.2"),sQuery(id+"F0.wireOp",EDGE,"E4.19.3"),sQuery(id+"F0.wireOp",EDGE,"E4.20.0"),sQuery(id+"F0.wireOp",EDGE,"E4.20.1"),sQuery(id+"F0.wireOp",EDGE,"E4.20.2"),sQuery(id+"F0.wireOp",EDGE,"E4.20.3"),sQuery(id+"F0.wireOp",EDGE,"E4.21.0"),sQuery(id+"F0.wireOp",EDGE,"E4.21.1"),sQuery(id+"F0.wireOp",EDGE,"E4.21.2"),sQuery(id+"F0.wireOp",EDGE,"E4.21.3"),sQuery(id+"F0.wireOp",EDGE,"E4.22.0"),sQuery(id+"F0.wireOp",EDGE,"E4.22.1"),sQuery(id+"F0.wireOp",EDGE,"E4.22.2"),sQuery(id+"F0.wireOp",EDGE,"E4.22.3"),sQuery(id+"F0.wireOp",EDGE,"E4.23.0"),sQuery(id+"F0.wireOp",EDGE,"E4.23.1"),sQuery(id+"F0.wireOp",EDGE,"E4.23.2"),sQuery(id+"F0.wireOp",EDGE,"E4.23.3"),sQuery(id+"F0.wireOp",EDGE,"E4.24.0"),sQuery(id+"F0.wireOp",EDGE,"E4.24.1"),sQuery(id+"F0.wireOp",EDGE,"E4.24.2"),sQuery(id+"F0.wireOp",EDGE,"E4.24.3"),sQuery(id+"F0.wireOp",EDGE,"E4.25.0"),sQuery(id+"F0.wireOp",EDGE,"E4.25.1"),sQuery(id+"F0.wireOp",EDGE,"E4.25.2"),sQuery(id+"F0.wireOp",EDGE,"E4.25.3"),sQuery(id+"F0.wireOp",EDGE,"E4.26.0"),sQuery(id+"F0.wireOp",EDGE,"E4.26.1"),sQuery(id+"F0.wireOp",EDGE,"E4.26.2"),sQuery(id+"F0.wireOp",EDGE,"E4.26.3"),sQuery(id+"F0.wireOp",EDGE,"E4.27.0"),sQuery(id+"F0.wireOp",EDGE,"E4.27.1"),sQuery(id+"F0.wireOp",EDGE,"E4.27.2"),sQuery(id+"F0.wireOp",EDGE,"E4.27.3"),sQuery(id+"F0.wireOp",EDGE,"E4.28.0"),sQuery(id+"F0.wireOp",EDGE,"E4.28.1"),sQuery(id+"F0.wireOp",EDGE,"E4.28.2"),sQuery(id+"F0.wireOp",EDGE,"E4.28.3"),sQuery(id+"F0.wireOp",EDGE,"E4.29.0"),sQuery(id+"F0.wireOp",EDGE,"E4.29.1"),sQuery(id+"F0.wireOp",EDGE,"E4.29.2"),sQuery(id+"F0.wireOp",EDGE,"E4.29.3"),sQuery(id+"F0.wireOp",EDGE,"E4.30.0"),sQuery(id+"F0.wireOp",EDGE,"E4.30.1"),sQuery(id+"F0.wireOp",EDGE,"E4.30.2"),sQuery(id+"F0.wireOp",EDGE,"E4.30.3"),sQuery(id+"F0.wireOp",EDGE,"E4.31.0"),sQuery(id+"F0.wireOp",EDGE,"E4.31.1"),sQuery(id+"F0.wireOp",EDGE,"E4.31.2"),sQuery(id+"F0.wireOp",EDGE,"E4.31.3"),sQuery(id+"F0.wireOp",EDGE,"E4.32.0"),sQuery(id+"F0.wireOp",EDGE,"E4.32.1"),sQuery(id+"F0.wireOp",EDGE,"E4.32.2"),sQuery(id+"F0.wireOp",EDGE,"E4.32.3"),sQuery(id+"F0.wireOp",EDGE,"E4.33.0"),sQuery(id+"F0.wireOp",EDGE,"E4.33.1"),sQuery(id+"F0.wireOp",EDGE,"E4.33.2"),sQuery(id+"F0.wireOp",EDGE,"E4.33.3"),sQuery(id+"F0.wireOp",EDGE,"E4.34.0"),sQuery(id+"F0.wireOp",EDGE,"E4.34.1"),sQuery(id+"F0.wireOp",EDGE,"E4.34.2"),sQuery(id+"F0.wireOp",EDGE,"E4.34.3"),sQuery(id+"F0.wireOp",EDGE,"E4.35.0"),sQuery(id+"F0.wireOp",EDGE,"E4.35.1"),sQuery(id+"F0.wireOp",EDGE,"E4.35.2"),sQuery(id+"F0.wireOp",EDGE,"E4.35.3"),sQuery(id+"F0.wireOp",EDGE,"E4.36.0"),sQuery(id+"F0.wireOp",EDGE,"E4.36.1"),sQuery(id+"F0.wireOp",EDGE,"E4.36.2"),sQuery(id+"F0.wireOp",EDGE,"E4.36.3"),sQuery(id+"F0.wireOp",EDGE,"E4.37.0"),sQuery(id+"F0.wireOp",EDGE,"E4.37.1"),sQuery(id+"F0.wireOp",EDGE,"E4.37.2"),sQuery(id+"F0.wireOp",EDGE,"E4.37.3"),sQuery(id+"F0.wireOp",EDGE,"E4.38.0"),sQuery(id+"F0.wireOp",EDGE,"E4.38.1"),sQuery(id+"F0.wireOp",EDGE,"E4.38.2"),sQuery(id+"F0.wireOp",EDGE,"E4.38.3"),sQuery(id+"F0.wireOp",EDGE,"E4.39.0"),sQuery(id+"F0.wireOp",EDGE,"E4.39.1"),sQuery(id+"F0.wireOp",EDGE,"E4.39.2"),sQuery(id+"F0.wireOp",EDGE,"E4.39.3"),sQuery(id+"F0.wireOp",EDGE,"E4.40.0"),sQuery(id+"F0.wireOp",EDGE,"E4.40.1"),sQuery(id+"F0.wireOp",EDGE,"E4.40.2"),sQuery(id+"F0.wireOp",EDGE,"E4.40.3"),sQuery(id+"F0.wireOp",EDGE,"E4.41.0"),sQuery(id+"F0.wireOp",EDGE,"E4.41.1"),sQuery(id+"F0.wireOp",EDGE,"E4.41.2"),sQuery(id+"F0.wireOp",EDGE,"E4.41.3"),sQuery(id+"F0.wireOp",EDGE,"E4.42.0"),sQuery(id+"F0.wireOp",EDGE,"E4.42.1"),sQuery(id+"F0.wireOp",EDGE,"E4.42.2"),sQuery(id+"F0.wireOp",EDGE,"E4.42.3"),sQuery(id+"F0.wireOp",EDGE,"E4.43.0"),sQuery(id+"F0.wireOp",EDGE,"E4.43.1"),sQuery(id+"F0.wireOp",EDGE,"E4.43.2"),sQuery(id+"F0.wireOp",EDGE,"E4.43.3"),sQuery(id+"F0.wireOp",EDGE,"E4.44.0"),sQuery(id+"F0.wireOp",EDGE,"E4.44.1"),sQuery(id+"F0.wireOp",EDGE,"E4.44.2"),sQuery(id+"F0.wireOp",EDGE,"E4.44.3"),sQuery(id+"F0.wireOp",EDGE,"E4.45.0"),sQuery(id+"F0.wireOp",EDGE,"E4.45.1"),sQuery(id+"F0.wireOp",EDGE,"E4.45.2"),sQuery(id+"F0.wireOp",EDGE,"E4.45.3"),sQuery(id+"F0.wireOp",EDGE,"E4.46.0"),sQuery(id+"F0.wireOp",EDGE,"E4.46.1"),sQuery(id+"F0.wireOp",EDGE,"E4.46.2"),sQuery(id+"F0.wireOp",EDGE,"E4.46.3"),sQuery(id+"F0.wireOp",EDGE,"E4.47.0"),sQuery(id+"F0.wireOp",EDGE,"E4.47.1"),sQuery(id+"F0.wireOp",EDGE,"E4.47.2"),sQuery(id+"F0.wireOp",EDGE,"E4.47.3"),sQuery(id+"F0.wireOp",EDGE,"E4.48.0"),sQuery(id+"F0.wireOp",EDGE,"E4.48.1"),sQuery(id+"F0.wireOp",EDGE,"E4.48.2"),sQuery(id+"F0.wireOp",EDGE,"E4.48.3"),sQuery(id+"F0.wireOp",EDGE,"E4.49.0"),sQuery(id+"F0.wireOp",EDGE,"E4.49.1"),sQuery(id+"F0.wireOp",EDGE,"E4.49.2"),sQuery(id+"F0.wireOp",EDGE,"E4.49.3"),sQuery(id+"F0.wireOp",EDGE,"E4.50.0"),sQuery(id+"F0.wireOp",EDGE,"E4.50.1"),sQuery(id+"F0.wireOp",EDGE,"E4.50.2"),sQuery(id+"F0.wireOp",EDGE,"E4.50.3"),sQuery(id+"F0.wireOp",EDGE,"E4.51.0"),sQuery(id+"F0.wireOp",EDGE,"E4.51.1"),sQuery(id+"F0.wireOp",EDGE,"E4.51.2"),sQuery(id+"F0.wireOp",EDGE,"E4.51.3"),sQuery(id+"F0.wireOp",EDGE,"E4.52.0"),sQuery(id+"F0.wireOp",EDGE,"E4.52.1"),sQuery(id+"F0.wireOp",EDGE,"E4.52.2"),sQuery(id+"F0.wireOp",EDGE,"E4.52.3"),sQuery(id+"F0.wireOp",EDGE,"E4.53.0"),sQuery(id+"F0.wireOp",EDGE,"E4.53.1"),sQuery(id+"F0.wireOp",EDGE,"E4.53.2"),sQuery(id+"F0.wireOp",EDGE,"E4.53.3"),sQuery(id+"F0.wireOp",EDGE,"E4.54.0"),sQuery(id+"F0.wireOp",EDGE,"E4.54.1"),sQuery(id+"F0.wireOp",EDGE,"E4.54.2"),sQuery(id+"F0.wireOp",EDGE,"E4.54.3"),sQuery(id+"F0.wireOp",EDGE,"E4.55.0"),sQuery(id+"F0.wireOp",EDGE,"E4.55.1"),sQuery(id+"F0.wireOp",EDGE,"E4.55.2"),sQuery(id+"F0.wireOp",EDGE,"E4.55.3"),sQuery(id+"F0.wireOp",EDGE,"E4.56.0"),sQuery(id+"F0.wireOp",EDGE,"E4.56.1"),sQuery(id+"F0.wireOp",EDGE,"E4.56.2"),sQuery(id+"F0.wireOp",EDGE,"E4.56.3"),sQuery(id+"F0.wireOp",EDGE,"E4.57.0"),sQuery(id+"F0.wireOp",EDGE,"E4.57.1"),sQuery(id+"F0.wireOp",EDGE,"E4.57.2"),sQuery(id+"F0.wireOp",EDGE,"E4.57.3"),sQuery(id+"F0.wireOp",EDGE,"E4.58.0"),sQuery(id+"F0.wireOp",EDGE,"E4.58.1"),sQuery(id+"F0.wireOp",EDGE,"E4.58.2"),sQuery(id+"F0.wireOp",EDGE,"E4.58.3"),sQuery(id+"F0.wireOp",EDGE,"E4.59.0"),sQuery(id+"F0.wireOp",EDGE,"E4.59.1"),sQuery(id+"F0.wireOp",EDGE,"E4.59.2"),sQuery(id+"F0.wireOp",EDGE,"E4.59.3"),sQuery(id+"F0.wireOp",EDGE,"E4.60.0"),sQuery(id+"F0.wireOp",EDGE,"E4.60.1"),sQuery(id+"F0.wireOp",EDGE,"E4.60.2"),sQuery(id+"F0.wireOp",EDGE,"E4.60.3"),sQuery(id+"F0.wireOp",EDGE,"E4.61.0"),sQuery(id+"F0.wireOp",EDGE,"E4.61.1"),sQuery(id+"F0.wireOp",EDGE,"E4.61.2"),sQuery(id+"F0.wireOp",EDGE,"E4.61.3"),sQuery(id+"F0.wireOp",EDGE,"E4.62.0"),sQuery(id+"F0.wireOp",EDGE,"E4.62.1"),sQuery(id+"F0.wireOp",EDGE,"E4.62.2"),sQuery(id+"F0.wireOp",EDGE,"E4.62.3"),sQuery(id+"F0.wireOp",EDGE,"E4.63.0"),sQuery(id+"F0.wireOp",EDGE,"E4.63.1"),sQuery(id+"F0.wireOp",EDGE,"E4.63.2"),sQuery(id+"F0.wireOp",EDGE,"E4.63.3"),sQuery(id+"F0.wireOp",EDGE,"E4.64.0"),sQuery(id+"F0.wireOp",EDGE,"E4.64.1"),sQuery(id+"F0.wireOp",EDGE,"E4.64.2"),sQuery(id+"F0.wireOp",EDGE,"E4.64.3"),sQuery(id+"F0.wireOp",EDGE,"E4.65.0"),sQuery(id+"F0.wireOp",EDGE,"E4.65.1"),sQuery(id+"F0.wireOp",EDGE,"E4.65.2"),sQuery(id+"F0.wireOp",EDGE,"E4.65.3"),sQuery(id+"F0.wireOp",EDGE,"E4.66.0"),sQuery(id+"F0.wireOp",EDGE,"E4.66.1"),sQuery(id+"F0.wireOp",EDGE,"E4.66.2"),sQuery(id+"F0.wireOp",EDGE,"E4.66.3"),sQuery(id+"F0.wireOp",EDGE,"E4.67.0"),sQuery(id+"F0.wireOp",EDGE,"E4.67.1"),sQuery(id+"F0.wireOp",EDGE,"E4.67.2"),sQuery(id+"F0.wireOp",EDGE,"E4.67.3"),sQuery(id+"F0.wireOp",EDGE,"E4.68.0"),sQuery(id+"F0.wireOp",EDGE,"E4.68.1"),sQuery(id+"F0.wireOp",EDGE,"E4.68.2"),sQuery(id+"F0.wireOp",EDGE,"E4.68.3"),sQuery(id+"F0.wireOp",EDGE,"E4.69.0"),sQuery(id+"F0.wireOp",EDGE,"E4.69.1"),sQuery(id+"F0.wireOp",EDGE,"E4.69.2"),sQuery(id+"F0.wireOp",EDGE,"E4.69.3"),sQuery(id+"F0.wireOp",EDGE,"E4.70.0"),sQuery(id+"F0.wireOp",EDGE,"E4.70.1"),sQuery(id+"F0.wireOp",EDGE,"E4.70.2"),sQuery(id+"F0.wireOp",EDGE,"E4.70.3"),sQuery(id+"F0.wireOp",EDGE,"E4.71.0"),sQuery(id+"F0.wireOp",EDGE,"E4.71.1"),sQuery(id+"F0.wireOp",EDGE,"E4.71.2"),sQuery(id+"F0.wireOp",EDGE,"E4.71.3"),sQuery(id+"F0.wireOp",EDGE,"E4.72.0"),sQuery(id+"F0.wireOp",EDGE,"E4.72.1"),sQuery(id+"F0.wireOp",EDGE,"E4.72.2"),sQuery(id+"F0.wireOp",EDGE,"E4.72.3"),sQuery(id+"F0.wireOp",EDGE,"E4.73.0"),sQuery(id+"F0.wireOp",EDGE,"E4.73.1"),sQuery(id+"F0.wireOp",EDGE,"E4.73.2"),sQuery(id+"F0.wireOp",EDGE,"E4.73.3"),sQuery(id+"F0.wireOp",EDGE,"E4.74.0"),sQuery(id+"F0.wireOp",EDGE,"E4.74.1"),sQuery(id+"F0.wireOp",EDGE,"E4.74.2"),sQuery(id+"F0.wireOp",EDGE,"E4.74.3"),sQuery(id+"F0.wireOp",EDGE,"E4.75.0"),sQuery(id+"F0.wireOp",EDGE,"E4.75.1"),sQuery(id+"F0.wireOp",EDGE,"E4.75.2"),sQuery(id+"F0.wireOp",EDGE,"E4.75.3"),sQuery(id+"F0.wireOp",EDGE,"E4.76.0"),sQuery(id+"F0.wireOp",EDGE,"E4.76.1"),sQuery(id+"F0.wireOp",EDGE,"E4.76.2"),sQuery(id+"F0.wireOp",EDGE,"E4.76.3"),sQuery(id+"F0.wireOp",EDGE,"E4.77.0"),sQuery(id+"F0.wireOp",EDGE,"E4.77.1"),sQuery(id+"F0.wireOp",EDGE,"E4.77.2"),sQuery(id+"F0.wireOp",EDGE,"E4.77.3"),sQuery(id+"F0.wireOp",EDGE,"E4.78.0"),sQuery(id+"F0.wireOp",EDGE,"E4.78.1"),sQuery(id+"F0.wireOp",EDGE,"E4.78.2"),sQuery(id+"F0.wireOp",EDGE,"E4.78.3"),sQuery(id+"F0.wireOp",EDGE,"E4.79.0"),sQuery(id+"F0.wireOp",EDGE,"E4.79.1"),sQuery(id+"F0.wireOp",EDGE,"E4.79.2"),sQuery(id+"F0.wireOp",EDGE,"E4.79.3"),sQuery(id+"F0.wireOp",EDGE,"E4.80.0"),sQuery(id+"F0.wireOp",EDGE,"E4.80.1"),sQuery(id+"F0.wireOp",EDGE,"E4.80.2"),sQuery(id+"F0.wireOp",EDGE,"E4.80.3"),sQuery(id+"F0.wireOp",EDGE,"E4.81.0"),sQuery(id+"F0.wireOp",EDGE,"E4.81.1"),sQuery(id+"F0.wireOp",EDGE,"E4.81.2"),sQuery(id+"F0.wireOp",EDGE,"E4.81.3"),sQuery(id+"F0.wireOp",EDGE,"E4.82.0"),sQuery(id+"F0.wireOp",EDGE,"E4.82.1"),sQuery(id+"F0.wireOp",EDGE,"E4.82.2"),sQuery(id+"F0.wireOp",EDGE,"E4.82.3"),sQuery(id+"F0.wireOp",EDGE,"E4.83.0"),sQuery(id+"F0.wireOp",EDGE,"E4.83.1"),sQuery(id+"F0.wireOp",EDGE,"E4.83.2"),sQuery(id+"F0.wireOp",EDGE,"E4.83.3"),sQuery(id+"F0.wireOp",EDGE,"E4.84.0"),sQuery(id+"F0.wireOp",EDGE,"E4.84.1"),sQuery(id+"F0.wireOp",EDGE,"E4.84.2"),sQuery(id+"F0.wireOp",EDGE,"E4.84.3"),sQuery(id+"F0.wireOp",EDGE,"E4.85.0"),sQuery(id+"F0.wireOp",EDGE,"E4.85.1"),sQuery(id+"F0.wireOp",EDGE,"E4.85.2"),sQuery(id+"F0.wireOp",EDGE,"E4.85.3"),sQuery(id+"F0.wireOp",EDGE,"E4.86.0"),sQuery(id+"F0.wireOp",EDGE,"E4.86.1"),sQuery(id+"F0.wireOp",EDGE,"E4.86.2"),sQuery(id+"F0.wireOp",EDGE,"E4.86.3"),sQuery(id+"F0.wireOp",EDGE,"E4.87.0"),sQuery(id+"F0.wireOp",EDGE,"E4.87.1"),sQuery(id+"F0.wireOp",EDGE,"E4.87.2"),sQuery(id+"F0.wireOp",EDGE,"E4.87.3"),sQuery(id+"F0.wireOp",EDGE,"E4.88.0"),sQuery(id+"F0.wireOp",EDGE,"E4.88.1"),sQuery(id+"F0.wireOp",EDGE,"E4.88.2"),sQuery(id+"F0.wireOp",EDGE,"E4.88.3"),sQuery(id+"F0.wireOp",EDGE,"E4.89.0"),sQuery(id+"F0.wireOp",EDGE,"E4.89.1"),sQuery(id+"F0.wireOp",EDGE,"E4.89.2"),sQuery(id+"F0.wireOp",EDGE,"E4.89.3"),sQuery(id+"F0.wireOp",EDGE,"E4.90.0"),sQuery(id+"F0.wireOp",EDGE,"E4.90.1"),sQuery(id+"F0.wireOp",EDGE,"E4.90.2"),sQuery(id+"F0.wireOp",EDGE,"E4.90.3"),sQuery(id+"F0.wireOp",EDGE,"E4.91.0"),sQuery(id+"F0.wireOp",EDGE,"E4.91.1"),sQuery(id+"F0.wireOp",EDGE,"E4.91.2"),sQuery(id+"F0.wireOp",EDGE,"E4.91.3"),sQuery(id+"F0.wireOp",EDGE,"E4.92.0"),sQuery(id+"F0.wireOp",EDGE,"E4.92.1"),sQuery(id+"F0.wireOp",EDGE,"E4.92.2"),sQuery(id+"F0.wireOp",EDGE,"E4.92.3"),sQuery(id+"F0.wireOp",EDGE,"E4.93.0"),sQuery(id+"F0.wireOp",EDGE,"E4.93.1"),sQuery(id+"F0.wireOp",EDGE,"E4.93.2"),sQuery(id+"F0.wireOp",EDGE,"E4.93.3"),sQuery(id+"F0.wireOp",EDGE,"E4.94.0"),sQuery(id+"F0.wireOp",EDGE,"E4.94.1"),sQuery(id+"F0.wireOp",EDGE,"E4.94.2"),sQuery(id+"F0.wireOp",EDGE,"E4.94.3"),sQuery(id+"F0.wireOp",EDGE,"E4.95.0"),sQuery(id+"F0.wireOp",EDGE,"E4.95.1"),sQuery(id+"F0.wireOp",EDGE,"E4.95.2"),sQuery(id+"F0.wireOp",EDGE,"E4.95.3"),sQuery(id+"F0.wireOp",EDGE,"E5")])],"isStart":true});
            chamfer(context, id + "F2", {"entities" : qUnion([Q0, Q1]), "width" : .5 * mm, "tangentPropagation" : true});
        }
    });
